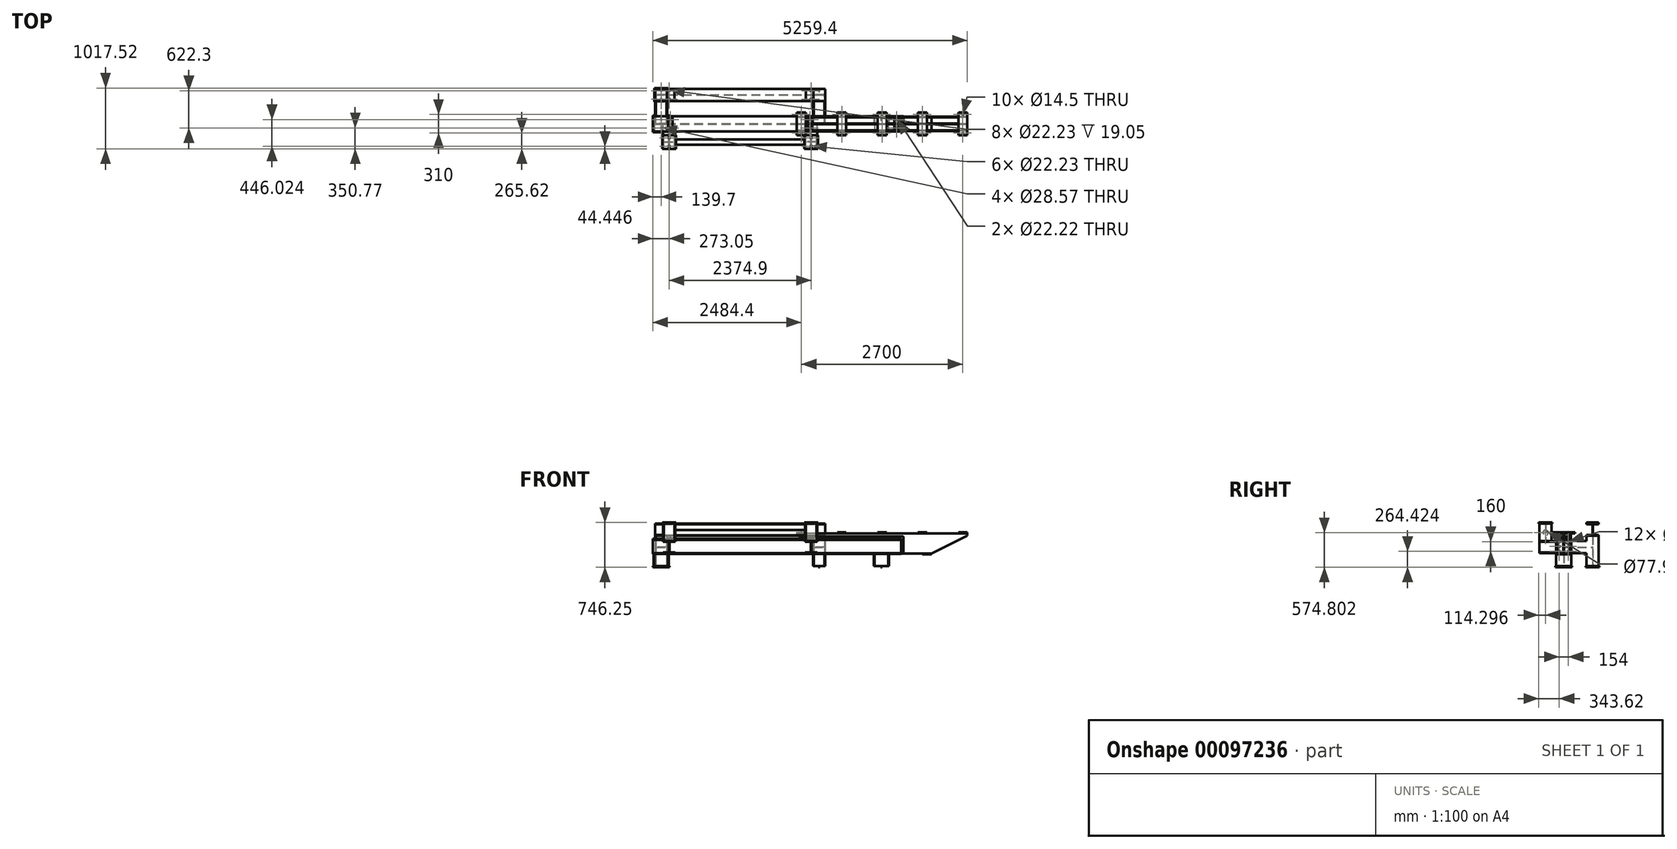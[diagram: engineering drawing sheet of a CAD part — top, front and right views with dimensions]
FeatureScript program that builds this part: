
annotation { "Feature Type Name" : "Feature", "Feature Type Description" : "" }
export const myFeature = defineFeature(function(context is Context, id is Id, definition is map)
    precondition{}
    {
        {
            var Q0;
            Q0=qCreatedBy(makeId("Top.planeOp"),FACE);
            var sketch = newSketch(context, id + "F0", { "sketchPlane" : qUnion([Q0])});
            skLineSegment(sketch, "E0.bottom", {"start": v(-1320.8, 241.3) * mm, "end": v(1320.8, 241.3) * mm, "construction": true});
            skLineSegment(sketch, "E0.top", {"start": v(-1320.8, -241.3) * mm, "end": v(1320.8, -241.3) * mm, "construction": true});
            skLineSegment(sketch, "E0.left", {"start": v(-1320.8, 241.3) * mm, "end": v(-1320.8, -241.3) * mm, "construction": true});
            skLineSegment(sketch, "E0.right", {"start": v(1320.8, 241.3) * mm, "end": v(1320.8, -241.3) * mm, "construction": true});
            skPoint(sketch, "E0.middle", {"position": v(0, 0) * mm});
            skLineSegment(sketch, "E1.bottom", {"start": v(-1435.1, 355.6) * mm, "end": v(-1206.5, 355.6) * mm});
            skLineSegment(sketch, "E1.top", {"start": v(-1435.1, 127) * mm, "end": v(-1206.5, 127) * mm});
            skLineSegment(sketch, "E1.left", {"start": v(-1435.1, 355.6) * mm, "end": v(-1435.1, 127) * mm});
            skLineSegment(sketch, "E1.right", {"start": v(-1206.5, 355.6) * mm, "end": v(-1206.5, 127) * mm});
            skPoint(sketch, "E1.middle", {"position": v(-1320.8, 241.3) * mm});
            skLineSegment(sketch, "E2", {"start": v(0, -413.23) * mm, "end": v(0, 639.03) * mm, "construction": true});
            skLineSegment(sketch, "E3", {"start": v(-1320.8, 355.6) * mm, "end": v(-1320.8, 127) * mm, "construction": true});
            skLineSegment(sketch, "E4", {"start": v(-1435.1, 241.3) * mm, "end": v(-1206.5, 241.3) * mm, "construction": true});
            skLineSegment(sketch, "E5.0", {"start": v(-1435.1, 311.15) * mm, "end": v(-1206.5, 311.15) * mm, "construction": true});
            skCircle(sketch, "E6", {"center": v(-1320.8, 311.15) * mm, "radius": 14.29 * mm});
            skCircle(sketch, "E7.MirrorC", {"center": v(-1320.8, 171.45) * mm, "radius": 14.29 * mm});
            skCircle(sketch, "E8.MirrorC", {"center": v(1320.8, 311.15) * mm, "radius": 14.29 * mm});
            skCircle(sketch, "E9.MirrorC", {"center": v(1320.8, 171.45) * mm, "radius": 14.29 * mm});
            skLineSegment(sketch, "E10.MirrorCS", {"start": v(1435.1, 311.15) * mm, "end": v(1206.5, 311.15) * mm, "construction": true});
            skLineSegment(sketch, "E11.MirrorCS", {"start": v(1435.1, 241.3) * mm, "end": v(1206.5, 241.3) * mm, "construction": true});
            skLineSegment(sketch, "E12.MirrorCS", {"start": v(1320.8, 355.6) * mm, "end": v(1320.8, 127) * mm, "construction": true});
            skLineSegment(sketch, "E13.MirrorCS", {"start": v(1435.1, 355.6) * mm, "end": v(1206.5, 355.6) * mm});
            skPoint(sketch, "E14.MirrorP", {"position": v(1320.8, 241.3) * mm});
            skLineSegment(sketch, "E15.MirrorCS", {"start": v(1206.5, 355.6) * mm, "end": v(1206.5, 127) * mm});
            skLineSegment(sketch, "E16.MirrorCS", {"start": v(1435.1, 127) * mm, "end": v(1206.5, 127) * mm});
            skLineSegment(sketch, "E17.MirrorCS", {"start": v(1435.1, 355.6) * mm, "end": v(1435.1, 127) * mm});
            skLineSegment(sketch, "E18.bottom", {"start": v(-1460.5, -381) * mm, "end": v(-1181.1, -381) * mm});
            skLineSegment(sketch, "E18.top", {"start": v(-1460.5, -101.6) * mm, "end": v(-1181.1, -101.6) * mm});
            skLineSegment(sketch, "E18.left", {"start": v(-1460.5, -381) * mm, "end": v(-1460.5, -101.6) * mm});
            skLineSegment(sketch, "E18.right", {"start": v(-1181.1, -381) * mm, "end": v(-1181.1, -101.6) * mm});
            skPoint(sketch, "E18.middle", {"position": v(-1320.8, -241.3) * mm});
            skLineSegment(sketch, "E19", {"start": v(-1320.8, -241.3) * mm, "end": v(-1460.5, -241.3) * mm, "construction": true});
            skLineSegment(sketch, "E20.0", {"start": v(-1320.8, -171.45) * mm, "end": v(-1460.5, -171.45) * mm, "construction": true});
            skCircle(sketch, "E21", {"center": v(-1320.8, -171.45) * mm, "radius": 14.29 * mm});
            skCircle(sketch, "E22.MirrorC", {"center": v(-1320.8, -311.15) * mm, "radius": 14.29 * mm});
            skLineSegment(sketch, "E23", {"start": v(-1320.8, -638.8) * mm, "end": v(-1320.8, -1011) * mm, "construction": true});
            skPoint(sketch, "E24.orphan", {"position": v(-1320.8, -381) * mm});
            skLineSegment(sketch, "E25.0", {"start": v(0, -638.8) * mm, "end": v(0, -1011) * mm, "construction": true});
            skLineSegment(sketch, "E26.0", {"start": v(1320.8, -638.8) * mm, "end": v(1320.8, -1011) * mm, "construction": true});
            skLineSegment(sketch, "E27.0", {"start": v(2362.2, -638.8) * mm, "end": v(2362.2, -1011) * mm, "construction": true});
            skLineSegment(sketch, "E28", {"start": v(-1320.8, -1011) * mm, "end": v(2362.2, -1011) * mm, "construction": true});
            skLineSegment(sketch, "E29", {"start": v(520.7, -1011) * mm, "end": v(520.7, -1354.57) * mm, "construction": true});
            skCircle(sketch, "E30.MirrorC", {"center": v(2362.2, -171.45) * mm, "radius": 14.29 * mm});
            skCircle(sketch, "E31.MirrorC", {"center": v(2362.2, -311.15) * mm, "radius": 14.29 * mm});
            skLineSegment(sketch, "E32.MirrorCS", {"start": v(2362.2, -171.45) * mm, "end": v(2501.9, -171.45) * mm, "construction": true});
            skLineSegment(sketch, "E33.MirrorCS", {"start": v(2501.9, -101.6) * mm, "end": v(2222.5, -101.6) * mm});
            skLineSegment(sketch, "E34.MirrorCS", {"start": v(2501.9, -381) * mm, "end": v(2222.5, -381) * mm});
            skLineSegment(sketch, "E35.MirrorCS", {"start": v(2362.2, -241.3) * mm, "end": v(2501.9, -241.3) * mm, "construction": true});
            skPoint(sketch, "E36.MirrorP", {"position": v(2362.2, -241.3) * mm});
            skLineSegment(sketch, "E37.MirrorCS", {"start": v(2222.5, -381) * mm, "end": v(2222.5, -101.6) * mm});
            skPoint(sketch, "E38.MirrorP", {"position": v(2362.2, -381) * mm});
            skLineSegment(sketch, "E39.MirrorCS", {"start": v(2501.9, -381) * mm, "end": v(2501.9, -101.6) * mm});
            skSolve(sketch);
        }
        {
            var Q0;
            Q0=makeQuery(id+"F0.imprint","IMPRINT",FACE,{"disambiguationData":[TD([[makeQuery(id+"F0.imprint","IMPRINT",EDGE,{"derivedFrom":sQuery(id+"F0.wireOp",EDGE,"E1.bottom")}),-1.0]])]});
            var Q1;
            Q1=makeQuery(id+"F0.imprint","IMPRINT",FACE,{"disambiguationData":[TD([[makeQuery(id+"F0.imprint","IMPRINT",EDGE,{"derivedFrom":sQuery(id+"F0.wireOp",EDGE,"E8.MirrorC")}),1.0]])]});
            var Q2;
            Q2=makeQuery(id+"F0.imprint","IMPRINT",FACE,{"disambiguationData":[TD([[makeQuery(id+"F0.imprint","IMPRINT",EDGE,{"derivedFrom":sQuery(id+"F0.wireOp",EDGE,"E30.MirrorC")}),1.0]])]});
            var Q3;
            Q3=makeQuery(id+"F0.imprint","IMPRINT",FACE,{"disambiguationData":[TD([[makeQuery(id+"F0.imprint","IMPRINT",EDGE,{"derivedFrom":sQuery(id+"F0.wireOp",EDGE,"E18.bottom")}),1.0]])]});
            extrude(context, id + "F1", {"entities" : qUnion([Q0, Q1, Q2, Q3]), "depth" : 19.05 * mm});
        }
        {
            var Q0;
            Q0=makeQuery(id+"F1.opExtrude","CAP_FACE",FACE,{"disambiguationData":[OSD([sQuery(id+"F0.wireOp",EDGE,"E1.bottom"),sQuery(id+"F0.wireOp",EDGE,"E1.top"),sQuery(id+"F0.wireOp",EDGE,"E1.left"),sQuery(id+"F0.wireOp",EDGE,"E1.right"),sQuery(id+"F0.wireOp",EDGE,"E6"),sQuery(id+"F0.wireOp",EDGE,"E7.MirrorC")])],"isStart":false});
            var sketch = newSketch(context, id + "F2", { "sketchPlane" : qUnion([Q0])});
            skLineSegment(sketch, "E40.0", {"start": v(-1435.1, 241.3) * mm, "end": v(-1206.5, 241.3) * mm, "construction": true});
            skLineSegment(sketch, "E41.0", {"start": v(-1320.8, 355.6) * mm, "end": v(-1320.8, 127) * mm, "construction": true});
            skLineSegment(sketch, "E42.bottom", {"start": v(-1422.4, 342.9) * mm, "end": v(-1411.35, 342.9) * mm});
            skLineSegment(sketch, "E42.top", {"start": v(-1422.4, 139.7) * mm, "end": v(-1411.35, 139.7) * mm});
            skLineSegment(sketch, "E42.left", {"start": v(-1422.4, 342.9) * mm, "end": v(-1422.4, 139.7) * mm});
            skLineSegment(sketch, "E42.right", {"start": v(-1219.2, 342.9) * mm, "end": v(-1219.2, 139.7) * mm, "construction": true});
            skPoint(sketch, "E42.middle", {"position": v(-1320.8, 241.3) * mm});
            skLineSegment(sketch, "E43.0", {"start": v(-1411.35, 342.9) * mm, "end": v(-1411.35, 251.27) * mm});
            skLineSegment(sketch, "E44.trimOffspring", {"start": v(-1405, 237.68) * mm, "end": v(-1320.8, 237.68) * mm});
            skLineSegment(sketch, "E45.MirrorCS", {"start": v(-1405, 244.92) * mm, "end": v(-1320.8, 244.92) * mm});
            skLineSegment(sketch, "E46.trimOffspring", {"start": v(-1411.35, 231.33) * mm, "end": v(-1411.35, 139.7) * mm});
            skPoint(sketch, "E47.visualSharp", {"position": v(-1411.35, 244.92) * mm});
            skArc(sketch, "E47.filletArc", {"start": v(-1411.35, 251.27) * mm, "mid": v(-1409.5, 246.78) * mm, "end": v(-1405, 244.92) * mm});
            skPoint(sketch, "E48.visualSharp", {"position": v(-1411.35, 237.68) * mm});
            skArc(sketch, "E48.filletArc", {"start": v(-1405, 237.68) * mm, "mid": v(-1409.5, 235.82) * mm, "end": v(-1411.35, 231.33) * mm});
            skArc(sketch, "E49.MirrorCS", {"start": v(-1236.6, 237.68) * mm, "mid": v(-1232.1, 235.82) * mm, "end": v(-1230.25, 231.33) * mm});
            skArc(sketch, "E50.MirrorCS", {"start": v(-1230.25, 251.27) * mm, "mid": v(-1232.1, 246.78) * mm, "end": v(-1236.6, 244.92) * mm});
            skPoint(sketch, "E51.MirrorP", {"position": v(-1230.25, 237.68) * mm});
            skPoint(sketch, "E52.MirrorP", {"position": v(-1230.25, 244.92) * mm});
            skLineSegment(sketch, "E53.MirrorCS", {"start": v(-1230.25, 342.9) * mm, "end": v(-1230.25, 251.27) * mm});
            skLineSegment(sketch, "E54.MirrorCS", {"start": v(-1236.6, 237.68) * mm, "end": v(-1320.8, 237.68) * mm});
            skLineSegment(sketch, "E55.MirrorCS", {"start": v(-1236.6, 244.92) * mm, "end": v(-1320.8, 244.92) * mm});
            skLineSegment(sketch, "E56.MirrorCS", {"start": v(-1219.2, 139.7) * mm, "end": v(-1230.25, 139.7) * mm});
            skLineSegment(sketch, "E57.MirrorCS", {"start": v(-1230.25, 231.33) * mm, "end": v(-1230.25, 139.7) * mm});
            skLineSegment(sketch, "E58.MirrorCS", {"start": v(-1219.2, 342.9) * mm, "end": v(-1230.25, 342.9) * mm});
            skLineSegment(sketch, "E59.MirrorCS", {"start": v(-1219.2, 342.9) * mm, "end": v(-1219.2, 139.7) * mm});
            skLineSegment(sketch, "E60.0", {"start": v(0, -413.23) * mm, "end": v(0, 639.03) * mm, "construction": true});
            skArc(sketch, "E61.MirrorCS", {"start": v(1411.35, 251.27) * mm, "mid": v(1409.5, 246.78) * mm, "end": v(1405, 244.92) * mm});
            skArc(sketch, "E62.MirrorCS", {"start": v(1405, 237.68) * mm, "mid": v(1409.5, 235.82) * mm, "end": v(1411.35, 231.33) * mm});
            skLineSegment(sketch, "E63.MirrorCS", {"start": v(1236.6, 244.92) * mm, "end": v(1320.8, 244.92) * mm});
            skArc(sketch, "E64.MirrorCS", {"start": v(1236.6, 237.68) * mm, "mid": v(1232.1, 235.82) * mm, "end": v(1230.25, 231.33) * mm});
            skLineSegment(sketch, "E65.MirrorCS", {"start": v(1422.4, 139.7) * mm, "end": v(1411.35, 139.7) * mm});
            skLineSegment(sketch, "E66.MirrorCS", {"start": v(1422.4, 342.9) * mm, "end": v(1411.35, 342.9) * mm});
            skArc(sketch, "E67.MirrorCS", {"start": v(1230.25, 251.27) * mm, "mid": v(1232.1, 246.78) * mm, "end": v(1236.6, 244.92) * mm});
            skLineSegment(sketch, "E68.MirrorCS", {"start": v(1236.6, 237.68) * mm, "end": v(1320.8, 237.68) * mm});
            skLineSegment(sketch, "E69.MirrorCS", {"start": v(1435.1, 241.3) * mm, "end": v(1206.5, 241.3) * mm, "construction": true});
            skLineSegment(sketch, "E70.MirrorCS", {"start": v(1405, 237.68) * mm, "end": v(1320.8, 237.68) * mm});
            skLineSegment(sketch, "E71.MirrorCS", {"start": v(1219.2, 342.9) * mm, "end": v(1230.25, 342.9) * mm});
            skLineSegment(sketch, "E72.MirrorCS", {"start": v(1219.2, 139.7) * mm, "end": v(1230.25, 139.7) * mm});
            skLineSegment(sketch, "E73.MirrorCS", {"start": v(1411.35, 342.9) * mm, "end": v(1411.35, 251.27) * mm});
            skLineSegment(sketch, "E74.MirrorCS", {"start": v(1405, 244.92) * mm, "end": v(1320.8, 244.92) * mm});
            skLineSegment(sketch, "E75.MirrorCS", {"start": v(1411.35, 231.33) * mm, "end": v(1411.35, 139.7) * mm});
            skPoint(sketch, "E76.MirrorP", {"position": v(1411.35, 237.68) * mm});
            skPoint(sketch, "E77.MirrorP", {"position": v(1320.8, 241.3) * mm});
            skLineSegment(sketch, "E78.MirrorCS", {"start": v(1219.2, 342.9) * mm, "end": v(1219.2, 139.7) * mm, "construction": true});
            skLineSegment(sketch, "E79.MirrorCS", {"start": v(1422.4, 342.9) * mm, "end": v(1422.4, 139.7) * mm});
            skPoint(sketch, "E80.MirrorP", {"position": v(1230.25, 237.68) * mm});
            skLineSegment(sketch, "E81.MirrorCS", {"start": v(1320.8, 355.6) * mm, "end": v(1320.8, 127) * mm, "construction": true});
            skPoint(sketch, "E82.MirrorP", {"position": v(1411.35, 244.92) * mm});
            skLineSegment(sketch, "E83.MirrorCS", {"start": v(1219.2, 342.9) * mm, "end": v(1219.2, 139.7) * mm});
            skLineSegment(sketch, "E84.MirrorCS", {"start": v(1230.25, 231.33) * mm, "end": v(1230.25, 139.7) * mm});
            skLineSegment(sketch, "E85.MirrorCS", {"start": v(1230.25, 342.9) * mm, "end": v(1230.25, 251.27) * mm});
            skPoint(sketch, "E86.MirrorP", {"position": v(1230.25, 244.92) * mm});
            skSolve(sketch);
        }
        {
            var Q0;
            Q0=qSketchRegion(id+"F2",true);
            extrude(context, id + "F3", {"entities" : qUnion([Q0]), "depth" : 504.95 * mm});
        }
        {
            var Q0;
            Q0=makeQuery(id+"F3.opExtrude","SWEPT_FACE",FACE,{"disambiguationData":[OSD([sQuery(id+"F2.wireOp",EDGE,"E79.MirrorCS")])]});
            var sketch = newSketch(context, id + "F4", { "sketchPlane" : qUnion([Q0])});
            skLineSegment(sketch, "E87.bottom", {"start": v(139.7, 524) * mm, "end": v(342.9, 524) * mm});
            skLineSegment(sketch, "E87.top", {"start": v(139.7, 727.2) * mm, "end": v(342.9, 727.2) * mm});
            skLineSegment(sketch, "E87.left", {"start": v(139.7, 524) * mm, "end": v(139.7, 535.05) * mm});
            skLineSegment(sketch, "E87.right", {"start": v(342.9, 524) * mm, "end": v(342.9, 535.05) * mm});
            skLineSegment(sketch, "E88", {"start": v(241.3, 727.2) * mm, "end": v(241.3, 524) * mm, "construction": true});
            skLineSegment(sketch, "E89.0", {"start": v(237.68, 709.8) * mm, "end": v(237.68, 541.4) * mm});
            skLineSegment(sketch, "E90.MirrorCS", {"start": v(244.92, 709.8) * mm, "end": v(244.92, 541.4) * mm});
            skLineSegment(sketch, "E91.0", {"start": v(139.7, 716.15) * mm, "end": v(231.33, 716.15) * mm});
            skLineSegment(sketch, "E92.0", {"start": v(139.7, 535.05) * mm, "end": v(231.33, 535.05) * mm});
            skLineSegment(sketch, "E93.trimOffspring", {"start": v(251.27, 716.15) * mm, "end": v(342.9, 716.15) * mm});
            skLineSegment(sketch, "E94.trimOffspring", {"start": v(251.27, 535.05) * mm, "end": v(342.9, 535.05) * mm});
            skLineSegment(sketch, "E95.trimOffspring", {"start": v(139.7, 716.15) * mm, "end": v(139.7, 727.2) * mm});
            skLineSegment(sketch, "E96.trimOffspring", {"start": v(342.9, 716.15) * mm, "end": v(342.9, 727.2) * mm});
            skPoint(sketch, "E97.newPointB", {"position": v(237.68, 524) * mm});
            skArc(sketch, "E97.filletArc", {"start": v(231.33, 535.05) * mm, "mid": v(235.82, 536.91) * mm, "end": v(237.68, 541.4) * mm});
            skPoint(sketch, "E98.newPointA", {"position": v(244.92, 524) * mm});
            skArc(sketch, "E98.filletArc", {"start": v(244.92, 541.4) * mm, "mid": v(246.78, 536.91) * mm, "end": v(251.27, 535.05) * mm});
            skPoint(sketch, "E99.newPointA", {"position": v(237.68, 727.2) * mm});
            skArc(sketch, "E99.filletArc", {"start": v(237.68, 709.8) * mm, "mid": v(235.82, 714.3) * mm, "end": v(231.33, 716.15) * mm});
            skPoint(sketch, "E100.newPointA", {"position": v(244.92, 727.2) * mm});
            skArc(sketch, "E100.filletArc", {"start": v(251.27, 716.15) * mm, "mid": v(246.78, 714.3) * mm, "end": v(244.92, 709.8) * mm});
            skSolve(sketch);
        }
        {
            var Q0;
            Q0=qSketchRegion(id+"F4",true);
            var Q1;
            Q1=makeQuery(id+"F3.opExtrude","SWEPT_FACE",FACE,{"disambiguationData":[OSD([sQuery(id+"F2.wireOp",EDGE,"E42.left")])]});
            extrude(context, id + "F5", {"entities" : qUnion([Q0]), "endBound" : BoundingType.UP_TO_SURFACE, "oppositeDirection" : true, "endBoundEntityFace" : qUnion([Q1]), "depth" : 25.4 * mm});
        }
        {
            var Q0;
            Q0=makeQuery(id+"F5.opExtrude","SWEPT_FACE",FACE,{"disambiguationData":[OSD([sQuery(id+"F4.wireOp",EDGE,"E87.top")])]});
            var sketch = newSketch(context, id + "F6", { "sketchPlane" : qUnion([Q0])});
            skLineSegment(sketch, "E101.0", {"start": v(0, -413.23) * mm, "end": v(0, 639.03) * mm, "construction": true});
            skLineSegment(sketch, "E102.0", {"start": v(-1187.45, -413.23) * mm, "end": v(-1187.45, 639.03) * mm, "construction": true});
            skLineSegment(sketch, "E103.0", {"start": v(-1225.55, 139.7) * mm, "end": v(-1225.55, 342.9) * mm});
            skLineSegment(sketch, "E104.0", {"start": v(-1098.55, 139.7) * mm, "end": v(-1098.55, 342.9) * mm});
            skLineSegment(sketch, "E105.0", {"start": v(-1422.4, 342.9) * mm, "end": v(1422.4, 342.9) * mm, "construction": true});
            skLineSegment(sketch, "E106.0.0", {"start": v(1225.55, 342.9) * mm, "end": v(-1225.55, 342.9) * mm});
            skLineSegment(sketch, "E106.0.1", {"start": v(-1422.4, 342.9) * mm, "end": v(-1422.4, 139.7) * mm});
            skLineSegment(sketch, "E106.0.2", {"start": v(-1225.55, 139.7) * mm, "end": v(-1098.55, 139.7) * mm});
            skLineSegment(sketch, "E106.0.3", {"start": v(1422.4, 139.7) * mm, "end": v(1422.4, 342.9) * mm});
            skLineSegment(sketch, "E107.trimOffspring", {"start": v(0, 139.7) * mm, "end": v(1225.55, 139.7) * mm});
            skLineSegment(sketch, "E108.0", {"start": v(-1320.8, 241.3) * mm, "end": v(1320.8, 241.3) * mm, "construction": true});
            skLineSegment(sketch, "E109.0", {"start": v(-1320.8, 311.15) * mm, "end": v(1320.8, 311.15) * mm, "construction": true});
            skCircle(sketch, "E110", {"center": v(-1187.45, 311.15) * mm, "radius": 11.11 * mm});
            skCircle(sketch, "E111.MirrorC", {"center": v(-1187.45, 171.45) * mm, "radius": 11.11 * mm});
            skCircle(sketch, "E112.MirrorC", {"center": v(1187.45, 311.15) * mm, "radius": 11.11 * mm});
            skCircle(sketch, "E113.MirrorC", {"center": v(1187.45, 171.45) * mm, "radius": 11.11 * mm});
            skLineSegment(sketch, "E114.MirrorCS", {"start": v(1225.55, 139.7) * mm, "end": v(1098.55, 139.7) * mm});
            skLineSegment(sketch, "E115.MirrorCS", {"start": v(1225.55, 139.7) * mm, "end": v(1225.55, 342.9) * mm});
            skLineSegment(sketch, "E116.MirrorCS", {"start": v(1098.55, 139.7) * mm, "end": v(1098.55, 342.9) * mm});
            skSolve(sketch);
        }
        {
            var Q0;
            Q0=qSketchRegion(id+"F6",true);
            extrude(context, id + "F7", {"entities" : qUnion([Q0]), "operationType" : NewBodyOperationType.ADD, "depth" : 19.05 * mm});
        }
        {
            var Q0;
            Q0=makeQuery(id+"F3.opExtrude","SWEPT_FACE",FACE,{"disambiguationData":[OSD([sQuery(id+"F2.wireOp",EDGE,"E44.trimOffspring"),sQuery(id+"F2.wireOp",EDGE,"E54.MirrorCS")])]});
            var sketch = newSketch(context, id + "F8", { "sketchPlane" : qUnion([Q0])});
            skLineSegment(sketch, "E117.0", {"start": v(-1460.5, 0) * mm, "end": v(-1181.1, 0) * mm, "construction": true});
            skLineSegment(sketch, "E118", {"start": v(-1320.8, 0) * mm, "end": v(-1320.8, 868.41) * mm, "construction": true});
            skLineSegment(sketch, "E119.0", {"start": v(-1422.4, 231.65) * mm, "end": v(-1411.35, 231.65) * mm});
            skLineSegment(sketch, "E120.0", {"start": v(-1422.4, 434.85) * mm, "end": v(-1411.35, 434.85) * mm});
            skLineSegment(sketch, "E121", {"start": v(-1422.4, 434.85) * mm, "end": v(-1422.4, 231.65) * mm});
            skLineSegment(sketch, "E122.0", {"start": v(-1411.35, 434.85) * mm, "end": v(-1411.35, 342.77) * mm});
            skLineSegment(sketch, "E123", {"start": v(-1411.35, 333.25) * mm, "end": v(-1320.8, 333.25) * mm, "construction": true});
            skLineSegment(sketch, "E124.0", {"start": v(-1405, 336.42) * mm, "end": v(-1320.8, 336.42) * mm});
            skLineSegment(sketch, "E125.MirrorCS", {"start": v(-1410.08, 330.07) * mm, "end": v(-1320.8, 330.07) * mm});
            skLineSegment(sketch, "E126.trimOffspring", {"start": v(-1411.35, 328.8) * mm, "end": v(-1411.35, 231.65) * mm});
            skPoint(sketch, "E127.newPointA", {"position": v(-1411.35, 336.42) * mm});
            skArc(sketch, "E127.filletArc", {"start": v(-1411.35, 342.77) * mm, "mid": v(-1409.5, 338.28) * mm, "end": v(-1405, 336.42) * mm});
            skPoint(sketch, "E128.visualSharp", {"position": v(-1411.35, 330.07) * mm});
            skArc(sketch, "E128.filletArc", {"start": v(-1410.08, 330.07) * mm, "mid": v(-1410.98, 329.7) * mm, "end": v(-1411.35, 328.8) * mm});
            skArc(sketch, "E129.MirrorCS", {"start": v(-1231.52, 330.07) * mm, "mid": v(-1230.62, 329.7) * mm, "end": v(-1230.25, 328.8) * mm});
            skArc(sketch, "E130.MirrorCS", {"start": v(-1230.25, 342.77) * mm, "mid": v(-1232.1, 338.28) * mm, "end": v(-1236.6, 336.42) * mm});
            skLineSegment(sketch, "E131.MirrorCS", {"start": v(-1219.2, 231.65) * mm, "end": v(-1230.25, 231.65) * mm});
            skLineSegment(sketch, "E132.MirrorCS", {"start": v(-1219.2, 434.85) * mm, "end": v(-1230.25, 434.85) * mm});
            skPoint(sketch, "E133.MirrorP", {"position": v(-1230.25, 336.42) * mm});
            skPoint(sketch, "E134.MirrorP", {"position": v(-1230.25, 330.07) * mm});
            skLineSegment(sketch, "E135.MirrorCS", {"start": v(-1230.25, 328.8) * mm, "end": v(-1230.25, 231.65) * mm});
            skLineSegment(sketch, "E136.MirrorCS", {"start": v(-1231.52, 330.07) * mm, "end": v(-1320.8, 330.07) * mm});
            skLineSegment(sketch, "E137.MirrorCS", {"start": v(-1219.2, 434.85) * mm, "end": v(-1219.2, 231.65) * mm});
            skLineSegment(sketch, "E138.MirrorCS", {"start": v(-1230.25, 434.85) * mm, "end": v(-1230.25, 342.77) * mm});
            skLineSegment(sketch, "E139.MirrorCS", {"start": v(-1230.25, 333.25) * mm, "end": v(-1320.8, 333.25) * mm, "construction": true});
            skLineSegment(sketch, "E140.MirrorCS", {"start": v(-1236.6, 336.42) * mm, "end": v(-1320.8, 336.42) * mm});
            skLineSegment(sketch, "E141", {"start": v(0, -179.83) * mm, "end": v(0, 965.66) * mm, "construction": true});
            skArc(sketch, "E142.MirrorCS", {"start": v(1411.35, 342.77) * mm, "mid": v(1409.5, 338.28) * mm, "end": v(1405, 336.42) * mm});
            skArc(sketch, "E143.MirrorCS", {"start": v(1410.08, 330.07) * mm, "mid": v(1410.98, 329.7) * mm, "end": v(1411.35, 328.8) * mm});
            skArc(sketch, "E144.MirrorCS", {"start": v(1230.25, 342.77) * mm, "mid": v(1232.1, 338.28) * mm, "end": v(1236.6, 336.42) * mm});
            skArc(sketch, "E145.MirrorCS", {"start": v(1231.52, 330.07) * mm, "mid": v(1230.62, 329.7) * mm, "end": v(1230.25, 328.8) * mm});
            skLineSegment(sketch, "E146.MirrorCS", {"start": v(1411.35, 333.25) * mm, "end": v(1320.8, 333.25) * mm, "construction": true});
            skLineSegment(sketch, "E147.MirrorCS", {"start": v(1219.2, 231.65) * mm, "end": v(1230.25, 231.65) * mm});
            skLineSegment(sketch, "E148.MirrorCS", {"start": v(1219.2, 434.85) * mm, "end": v(1230.25, 434.85) * mm});
            skLineSegment(sketch, "E149.MirrorCS", {"start": v(1422.4, 231.65) * mm, "end": v(1411.35, 231.65) * mm});
            skLineSegment(sketch, "E150.MirrorCS", {"start": v(1422.4, 434.85) * mm, "end": v(1411.35, 434.85) * mm});
            skLineSegment(sketch, "E151.MirrorCS", {"start": v(1405, 336.42) * mm, "end": v(1320.8, 336.42) * mm});
            skLineSegment(sketch, "E152.MirrorCS", {"start": v(1410.08, 330.07) * mm, "end": v(1320.8, 330.07) * mm});
            skLineSegment(sketch, "E153.MirrorCS", {"start": v(1230.25, 333.25) * mm, "end": v(1320.8, 333.25) * mm, "construction": true});
            skLineSegment(sketch, "E154.MirrorCS", {"start": v(1231.52, 330.07) * mm, "end": v(1320.8, 330.07) * mm});
            skLineSegment(sketch, "E155.MirrorCS", {"start": v(1236.6, 336.42) * mm, "end": v(1320.8, 336.42) * mm});
            skLineSegment(sketch, "E156.MirrorCS", {"start": v(1411.35, 328.8) * mm, "end": v(1411.35, 231.65) * mm});
            skPoint(sketch, "E157.MirrorP", {"position": v(1411.35, 330.07) * mm});
            skPoint(sketch, "E158.MirrorP", {"position": v(1411.35, 336.42) * mm});
            skLineSegment(sketch, "E159.MirrorCS", {"start": v(1422.4, 434.85) * mm, "end": v(1422.4, 231.65) * mm});
            skLineSegment(sketch, "E160.MirrorCS", {"start": v(1411.35, 434.85) * mm, "end": v(1411.35, 342.77) * mm});
            skLineSegment(sketch, "E161.MirrorCS", {"start": v(1230.25, 434.85) * mm, "end": v(1230.25, 342.77) * mm});
            skLineSegment(sketch, "E162.MirrorCS", {"start": v(1230.25, 328.8) * mm, "end": v(1230.25, 231.65) * mm});
            skPoint(sketch, "E163.MirrorP", {"position": v(1230.25, 330.07) * mm});
            skPoint(sketch, "E164.MirrorP", {"position": v(1230.25, 336.42) * mm});
            skLineSegment(sketch, "E165.MirrorCS", {"start": v(1219.2, 434.85) * mm, "end": v(1219.2, 231.65) * mm});
            skSolve(sketch);
        }
        {
            var Q0;
            Q0=qSketchRegion(id+"F8",true);
            extrude(context, id + "F9", {"entities" : qUnion([Q0]), "operationType" : NewBodyOperationType.ADD, "depth" : 482.6 * mm});
        }
        {
            var Q0;
            Q0=qCreatedBy(makeId("Right.planeOp"),FACE);
            cPlane(context, id + "F10", {"entities" : qUnion([Q0]), "cplaneType" : CPlaneType.OFFSET, "offset" : 2692.4 * mm, "width" : 152.4 * mm, "height" : 152.4 * mm});
        }
        {
            var Q0;
            Q0=qCreatedBy(id+"F10.planeOp",FACE);
            var sketch = newSketch(context, id + "F11", { "sketchPlane" : qUnion([Q0])});
            skLineSegment(sketch, "E166.0", {"start": v(-381, 19.05) * mm, "end": v(-101.6, 19.05) * mm, "construction": true});
            skLineSegment(sketch, "E167", {"start": v(-241.3, 19.05) * mm, "end": v(-241.3, 468.37) * mm, "construction": true});
            skLineSegment(sketch, "E168.0", {"start": v(-381, 217.42) * mm, "end": v(-101.6, 217.42) * mm, "construction": true});
            skLineSegment(sketch, "E169.bottom", {"start": v(-368.3, 217.42) * mm, "end": v(-114.3, 217.42) * mm});
            skLineSegment(sketch, "E169.top", {"start": v(-368.3, 471.42) * mm, "end": v(-114.3, 471.42) * mm});
            skLineSegment(sketch, "E169.left", {"start": v(-368.3, 217.42) * mm, "end": v(-368.3, 231.65) * mm});
            skLineSegment(sketch, "E169.right", {"start": v(-114.3, 217.42) * mm, "end": v(-114.3, 231.65) * mm});
            skLineSegment(sketch, "E170.0", {"start": v(-368.3, 457.2) * mm, "end": v(-254, 457.2) * mm});
            skLineSegment(sketch, "E171.0", {"start": v(-368.3, 231.65) * mm, "end": v(-254, 231.65) * mm});
            skLineSegment(sketch, "E172.0", {"start": v(-234.95, 238) * mm, "end": v(-234.95, 450.85) * mm});
            skLineSegment(sketch, "E173.MirrorCS", {"start": v(-247.65, 238) * mm, "end": v(-247.65, 450.85) * mm});
            skLineSegment(sketch, "E174.trimOffspring", {"start": v(-368.3, 457.2) * mm, "end": v(-368.3, 471.42) * mm});
            skLineSegment(sketch, "E175.trimOffspring", {"start": v(-114.3, 457.2) * mm, "end": v(-114.3, 471.42) * mm});
            skLineSegment(sketch, "E176.trimOffspring", {"start": v(-228.6, 457.2) * mm, "end": v(-114.3, 457.2) * mm});
            skLineSegment(sketch, "E177.trimOffspring", {"start": v(-228.6, 231.65) * mm, "end": v(-114.3, 231.65) * mm});
            skPoint(sketch, "E178.newPointB", {"position": v(-247.65, 468.37) * mm});
            skArc(sketch, "E178.filletArc", {"start": v(-247.65, 450.85) * mm, "mid": v(-249.5, 455.34) * mm, "end": v(-254, 457.2) * mm});
            skPoint(sketch, "E179.newPointB", {"position": v(-234.95, 468.37) * mm});
            skArc(sketch, "E179.filletArc", {"start": v(-228.6, 457.2) * mm, "mid": v(-233.1, 455.34) * mm, "end": v(-234.95, 450.85) * mm});
            skPoint(sketch, "E180.newPointB", {"position": v(-234.95, 19.05) * mm});
            skArc(sketch, "E180.filletArc", {"start": v(-234.95, 238) * mm, "mid": v(-233.1, 233.5) * mm, "end": v(-228.6, 231.65) * mm});
            skPoint(sketch, "E181.newPointA", {"position": v(-247.65, 19.05) * mm});
            skArc(sketch, "E181.filletArc", {"start": v(-254, 231.65) * mm, "mid": v(-249.5, 233.5) * mm, "end": v(-247.65, 238) * mm});
            skSolve(sketch);
        }
        {
            var Q0;
            Q0=qSketchRegion(id+"F11",true);
            extrude(context, id + "F12", {"entities" : qUnion([Q0]), "oppositeDirection" : true, "depth" : 4152.9 * mm});
        }
        {
            var Q0;
            Q0=makeQuery(id+"F1.opExtrude","CAP_FACE",FACE,{"disambiguationData":[OSD([sQuery(id+"F0.wireOp",EDGE,"E18.bottom"),sQuery(id+"F0.wireOp",EDGE,"E18.top"),sQuery(id+"F0.wireOp",EDGE,"E18.left"),sQuery(id+"F0.wireOp",EDGE,"E18.right"),sQuery(id+"F0.wireOp",EDGE,"E21"),sQuery(id+"F0.wireOp",EDGE,"E22.MirrorC")])],"isStart":false});
            var sketch = newSketch(context, id + "F13", { "sketchPlane" : qUnion([Q0])});
            skLineSegment(sketch, "E182.bottom", {"start": v(-1447.8, -114.3) * mm, "end": v(-1433.58, -114.3) * mm});
            skLineSegment(sketch, "E182.top", {"start": v(-1447.8, -368.3) * mm, "end": v(-1433.58, -368.3) * mm});
            skLineSegment(sketch, "E182.left", {"start": v(-1447.8, -114.3) * mm, "end": v(-1447.8, -368.3) * mm});
            skLineSegment(sketch, "E182.right", {"start": v(-1193.8, -114.3) * mm, "end": v(-1193.8, -368.3) * mm});
            skPoint(sketch, "E182.middle", {"position": v(-1320.8, -241.3) * mm});
            skLineSegment(sketch, "E183.0", {"start": v(-1433.58, -114.3) * mm, "end": v(-1433.58, -236.98) * mm});
            skLineSegment(sketch, "E184.0", {"start": v(-1208.02, -114.3) * mm, "end": v(-1208.02, -236.98) * mm});
            skLineSegment(sketch, "E185.trimOffspring", {"start": v(-1208.02, -114.3) * mm, "end": v(-1193.8, -114.3) * mm});
            skLineSegment(sketch, "E186.trimOffspring", {"start": v(-1208.02, -368.3) * mm, "end": v(-1193.8, -368.3) * mm});
            skLineSegment(sketch, "E187.0", {"start": v(-1208.02, -236.98) * mm, "end": v(-1433.58, -236.98) * mm});
            skLineSegment(sketch, "E188.MirrorCS", {"start": v(-1208.02, -245.62) * mm, "end": v(-1433.58, -245.62) * mm});
            skPoint(sketch, "E189.orphan", {"position": v(-1460.5, -236.98) * mm});
            skPoint(sketch, "E190.orphan", {"position": v(-1460.5, -245.62) * mm});
            skLineSegment(sketch, "E191.trimOffspring", {"start": v(-1433.58, -245.62) * mm, "end": v(-1433.58, -368.3) * mm});
            skPoint(sketch, "E192.orphan", {"position": v(-1320.8, -236.98) * mm});
            skPoint(sketch, "E193.orphan", {"position": v(-1320.8, -245.62) * mm});
            skLineSegment(sketch, "E194.trimOffspring", {"start": v(-1208.02, -245.62) * mm, "end": v(-1208.02, -368.3) * mm});
            skLineSegment(sketch, "E195.MirrorCS", {"start": v(2489.2, -368.3) * mm, "end": v(2474.98, -368.3) * mm});
            skLineSegment(sketch, "E196.MirrorCS", {"start": v(2489.2, -114.3) * mm, "end": v(2474.98, -114.3) * mm});
            skLineSegment(sketch, "E197.MirrorCS", {"start": v(2249.42, -368.3) * mm, "end": v(2235.2, -368.3) * mm});
            skLineSegment(sketch, "E198.MirrorCS", {"start": v(2249.42, -114.3) * mm, "end": v(2235.2, -114.3) * mm});
            skPoint(sketch, "E199.MirrorP", {"position": v(2362.2, -245.62) * mm});
            skPoint(sketch, "E200.MirrorP", {"position": v(2362.2, -236.98) * mm});
            skLineSegment(sketch, "E201.MirrorCS", {"start": v(2249.42, -245.62) * mm, "end": v(2474.98, -245.62) * mm});
            skPoint(sketch, "E202.MirrorP", {"position": v(2501.9, -236.98) * mm});
            skLineSegment(sketch, "E203.MirrorCS", {"start": v(2249.42, -236.98) * mm, "end": v(2474.98, -236.98) * mm});
            skPoint(sketch, "E204.MirrorP", {"position": v(2362.2, -241.3) * mm});
            skPoint(sketch, "E205.MirrorP", {"position": v(2501.9, -245.62) * mm});
            skLineSegment(sketch, "E206.MirrorCS", {"start": v(2249.42, -245.62) * mm, "end": v(2249.42, -368.3) * mm});
            skLineSegment(sketch, "E207.MirrorCS", {"start": v(2474.98, -245.62) * mm, "end": v(2474.98, -368.3) * mm});
            skLineSegment(sketch, "E208.MirrorCS", {"start": v(2249.42, -114.3) * mm, "end": v(2249.42, -236.98) * mm});
            skLineSegment(sketch, "E209.MirrorCS", {"start": v(2474.98, -114.3) * mm, "end": v(2474.98, -236.98) * mm});
            skLineSegment(sketch, "E210.MirrorCS", {"start": v(2235.2, -114.3) * mm, "end": v(2235.2, -368.3) * mm});
            skLineSegment(sketch, "E211.MirrorCS", {"start": v(2489.2, -114.3) * mm, "end": v(2489.2, -368.3) * mm});
            skSolve(sketch);
        }
        {
            var Q0;
            Q0=qSketchRegion(id+"F13",true);
            extrude(context, id + "F14", {"entities" : qUnion([Q0]), "depth" : 198.37 * mm});
        }
        {
            var Q0;
            Q0=makeQuery(id+"F12.opExtrude","SWEPT_FACE",FACE,{"disambiguationData":[OSD([sQuery(id+"F11.wireOp",EDGE,"E169.top")])]});
            var sketch = newSketch(context, id + "F15", { "sketchPlane" : qUnion([Q0])});
            skLineSegment(sketch, "E212.0", {"start": v(-1615.4, -241.3) * mm, "end": v(2831.5, -241.3) * mm, "construction": true});
            skLineSegment(sketch, "E213.0", {"start": v(0, -413.23) * mm, "end": v(0, 639.03) * mm, "construction": true});
            skPoint(sketch, "E214.orphan", {"position": v(-1320.8, -241.3) * mm});
            skLineSegment(sketch, "E215.0", {"start": v(-1168.4, -689.85) * mm, "end": v(-1168.4, 639.03) * mm, "construction": true});
            skLineSegment(sketch, "E216.0", {"start": v(-1130.3, -355.6) * mm, "end": v(-1130.3, -127) * mm});
            skLineSegment(sketch, "E217.0", {"start": v(-1206.5, -127) * mm, "end": v(-1130.3, -127) * mm});
            skLineSegment(sketch, "E218.0", {"start": v(-1615.4, -171.45) * mm, "end": v(2831.5, -171.45) * mm, "construction": true});
            skLineSegment(sketch, "E219.MirrorCS", {"start": v(-1206.5, -355.6) * mm, "end": v(-1130.3, -355.6) * mm});
            skLineSegment(sketch, "E220.MirrorCS", {"start": v(-1206.5, -355.6) * mm, "end": v(-1206.5, -127) * mm});
            skPoint(sketch, "E221.orphan", {"position": v(-1130.3, 639.03) * mm});
            skPoint(sketch, "E222.orphan", {"position": v(-1206.5, 639.03) * mm});
            skPoint(sketch, "E223.orphan", {"position": v(-1615.4, -127) * mm});
            skPoint(sketch, "E224.orphan", {"position": v(-1615.4, -355.6) * mm});
            skPoint(sketch, "E225.orphan", {"position": v(-1206.5, -689.85) * mm});
            skPoint(sketch, "E226.orphan", {"position": v(-1130.3, -689.85) * mm});
            skCircle(sketch, "E227", {"center": v(-1168.4, -171.45) * mm, "radius": 11.11 * mm});
            skCircle(sketch, "E228.MirrorC", {"center": v(-1168.4, -311.15) * mm, "radius": 11.11 * mm});
            skLineSegment(sketch, "E229.1.0.0", {"start": v(1130.3, -355.6) * mm, "end": v(1130.3, -127) * mm});
            skLineSegment(sketch, "E229.1.0.1", {"start": v(1130.3, -355.6) * mm, "end": v(1206.5, -355.6) * mm});
            skLineSegment(sketch, "E229.1.0.2", {"start": v(1130.3, -127) * mm, "end": v(1206.5, -127) * mm});
            skLineSegment(sketch, "E229.1.0.3", {"start": v(1206.5, -355.6) * mm, "end": v(1206.5, -127) * mm});
            skCircle(sketch, "E229.1.0.4", {"center": v(1168.4, -171.45) * mm, "radius": 11.11 * mm});
            skCircle(sketch, "E229.1.0.5", {"center": v(1168.4, -311.15) * mm, "radius": 11.11 * mm});
            skLineSegment(sketch, "E229.direction1", {"start": v(-1206.5, -355.6) * mm, "end": v(1130.3, -355.6) * mm, "construction": true});
            skLineSegment(sketch, "E230.1.0.1", {"start": v(2578.1, -355.6) * mm, "end": v(2578.1, -127) * mm});
            skLineSegment(sketch, "E230.1.0.2", {"start": v(2654.3, -355.6) * mm, "end": v(2654.3, -127) * mm});
            skCircle(sketch, "E230.1.0.3", {"center": v(2616.2, -311.15) * mm, "radius": 11.11 * mm});
            skCircle(sketch, "E230.1.0.4", {"center": v(2616.2, -171.45) * mm, "radius": 11.11 * mm});
            skLineSegment(sketch, "E230.1.0.5", {"start": v(2578.1, -355.6) * mm, "end": v(2654.3, -355.6) * mm});
            skLineSegment(sketch, "E230.1.0.6", {"start": v(2578.1, -127) * mm, "end": v(2654.3, -127) * mm});
            skLineSegment(sketch, "E230.direction1", {"start": v(1320.8, -241.3) * mm, "end": v(2768.6, -241.3) * mm, "construction": true});
            skSolve(sketch);
        }
        {
            var Q0;
            Q0=qSketchRegion(id+"F15",true);
            extrude(context, id + "F16", {"entities" : qUnion([Q0]), "operationType" : NewBodyOperationType.ADD, "depth" : 19.05 * mm});
        }
        {
            var Q0;
            Q0=makeQuery(id+"F12.opExtrude","SWEPT_FACE",FACE,{"disambiguationData":[OSD([sQuery(id+"F11.wireOp",EDGE,"E173.MirrorCS")])]});
            var sketch = newSketch(context, id + "F17", { "sketchPlane" : qUnion([Q0])});
            skLineSegment(sketch, "E231", {"start": v(0, -262.73) * mm, "end": v(0, 1224.7) * mm, "construction": true});
            skLineSegment(sketch, "E232.0", {"start": v(-1320.8, 0) * mm, "end": v(1320.8, 0) * mm, "construction": true});
            skLineSegment(sketch, "E233.0", {"start": v(-1320.8, 231.9) * mm, "end": v(1320.8, 231.9) * mm, "construction": true});
            skLineSegment(sketch, "E234.0", {"start": v(-1187.45, -262.73) * mm, "end": v(-1187.45, 1224.7) * mm, "construction": true});
            skLineSegment(sketch, "E235.0", {"start": v(-1320.8, 333.5) * mm, "end": v(1320.8, 333.5) * mm, "construction": true});
            skLineSegment(sketch, "E236.bottom", {"start": v(-1289.05, 435.1) * mm, "end": v(-1085.85, 435.1) * mm});
            skLineSegment(sketch, "E236.top", {"start": v(-1289.05, 231.9) * mm, "end": v(-1085.85, 231.9) * mm});
            skLineSegment(sketch, "E236.left", {"start": v(-1289.05, 435.1) * mm, "end": v(-1289.05, 424.05) * mm});
            skLineSegment(sketch, "E236.right", {"start": v(-1085.85, 435.1) * mm, "end": v(-1085.85, 424.05) * mm});
            skPoint(sketch, "E236.middle", {"position": v(-1187.45, 333.5) * mm});
            skLineSegment(sketch, "E237.0", {"start": v(-1289.05, 424.05) * mm, "end": v(-1197.36, 424.05) * mm});
            skLineSegment(sketch, "E238.MirrorCS", {"start": v(-1289.05, 242.95) * mm, "end": v(-1197.36, 242.95) * mm});
            skLineSegment(sketch, "E239.0", {"start": v(-1183.9, 249.3) * mm, "end": v(-1183.9, 417.7) * mm});
            skLineSegment(sketch, "E240.MirrorCS", {"start": v(-1191, 249.3) * mm, "end": v(-1191, 417.7) * mm});
            skLineSegment(sketch, "E241", {"start": v(-1177.54, 424.05) * mm, "end": v(-1085.85, 424.05) * mm});
            skLineSegment(sketch, "E242", {"start": v(-1177.54, 242.95) * mm, "end": v(-1085.85, 242.95) * mm});
            skPoint(sketch, "E243.newPointB", {"position": v(-1191, 1224.7) * mm});
            skArc(sketch, "E243.filletArc", {"start": v(-1191, 417.7) * mm, "mid": v(-1192.87, 422.2) * mm, "end": v(-1197.36, 424.05) * mm});
            skPoint(sketch, "E244.newPointA", {"position": v(-1191, -262.73) * mm});
            skArc(sketch, "E244.filletArc", {"start": v(-1197.36, 242.95) * mm, "mid": v(-1192.87, 244.81) * mm, "end": v(-1191, 249.3) * mm});
            skPoint(sketch, "E245.newPointA", {"position": v(-1183.9, -262.73) * mm});
            skArc(sketch, "E245.filletArc", {"start": v(-1183.9, 249.3) * mm, "mid": v(-1182.03, 244.81) * mm, "end": v(-1177.54, 242.95) * mm});
            skPoint(sketch, "E246.newPointB", {"position": v(-1183.9, 1224.7) * mm});
            skArc(sketch, "E246.filletArc", {"start": v(-1177.54, 424.05) * mm, "mid": v(-1182.03, 422.2) * mm, "end": v(-1183.9, 417.7) * mm});
            skLineSegment(sketch, "E247.trimOffspring", {"start": v(-1289.05, 242.95) * mm, "end": v(-1289.05, 231.9) * mm});
            skLineSegment(sketch, "E248.trimOffspring", {"start": v(-1085.85, 242.95) * mm, "end": v(-1085.85, 231.9) * mm});
            skArc(sketch, "E249.MirrorCS", {"start": v(1177.54, 424.05) * mm, "mid": v(1182.03, 422.2) * mm, "end": v(1183.9, 417.7) * mm});
            skArc(sketch, "E250.MirrorCS", {"start": v(1183.9, 249.3) * mm, "mid": v(1182.03, 244.81) * mm, "end": v(1177.54, 242.95) * mm});
            skArc(sketch, "E251.MirrorCS", {"start": v(1197.36, 242.95) * mm, "mid": v(1192.87, 244.81) * mm, "end": v(1191, 249.3) * mm});
            skArc(sketch, "E252.MirrorCS", {"start": v(1191, 417.7) * mm, "mid": v(1192.87, 422.2) * mm, "end": v(1197.36, 424.05) * mm});
            skLineSegment(sketch, "E253.MirrorCS", {"start": v(1085.85, 242.95) * mm, "end": v(1085.85, 231.9) * mm});
            skLineSegment(sketch, "E254.MirrorCS", {"start": v(1183.9, 249.3) * mm, "end": v(1183.9, 417.7) * mm});
            skLineSegment(sketch, "E255.MirrorCS", {"start": v(1289.05, 242.95) * mm, "end": v(1289.05, 231.9) * mm});
            skLineSegment(sketch, "E256.MirrorCS", {"start": v(1085.85, 435.1) * mm, "end": v(1085.85, 424.05) * mm});
            skLineSegment(sketch, "E257.MirrorCS", {"start": v(1289.05, 435.1) * mm, "end": v(1289.05, 424.05) * mm});
            skLineSegment(sketch, "E258.MirrorCS", {"start": v(1289.05, 242.95) * mm, "end": v(1197.36, 242.95) * mm});
            skLineSegment(sketch, "E259.MirrorCS", {"start": v(1289.05, 424.05) * mm, "end": v(1197.36, 424.05) * mm});
            skLineSegment(sketch, "E260.MirrorCS", {"start": v(1289.05, 435.1) * mm, "end": v(1085.85, 435.1) * mm});
            skLineSegment(sketch, "E261.MirrorCS", {"start": v(1177.54, 424.05) * mm, "end": v(1085.85, 424.05) * mm});
            skLineSegment(sketch, "E262.MirrorCS", {"start": v(1289.05, 231.9) * mm, "end": v(1085.85, 231.9) * mm});
            skLineSegment(sketch, "E263.MirrorCS", {"start": v(1177.54, 242.95) * mm, "end": v(1085.85, 242.95) * mm});
            skLineSegment(sketch, "E264.MirrorCS", {"start": v(1191, 249.3) * mm, "end": v(1191, 417.7) * mm});
            skPoint(sketch, "E265.MirrorP", {"position": v(1187.45, 333.5) * mm});
            skSolve(sketch);
        }
        {
            var Q0;
            Q0=qSketchRegion(id+"F17",true);
            extrude(context, id + "F18", {"entities" : qUnion([Q0]), "depth" : 401.57 * mm});
        }
        {
            var Q0;
            Q0=makeQuery(id+"F18.opExtrude","SWEPT_FACE",FACE,{"disambiguationData":[OSD([sQuery(id+"F17.wireOp",EDGE,"E236.bottom")])]});
            var sketch = newSketch(context, id + "F19", { "sketchPlane" : qUnion([Q0])});
            skLineSegment(sketch, "E266.bottom", {"start": v(-1289.05, -649.22) * mm, "end": v(-1278, -649.22) * mm});
            skLineSegment(sketch, "E266.top", {"start": v(-1289.05, -446.02) * mm, "end": v(-1278, -446.02) * mm});
            skLineSegment(sketch, "E266.left", {"start": v(-1289.05, -649.22) * mm, "end": v(-1289.05, -446.02) * mm});
            skLineSegment(sketch, "E266.right", {"start": v(-1085.85, -649.22) * mm, "end": v(-1085.85, -446.02) * mm});
            skLineSegment(sketch, "E267", {"start": v(-1187.45, -446.02) * mm, "end": v(-1187.45, -700.9) * mm, "construction": true});
            skLineSegment(sketch, "E268", {"start": v(-1289.05, -547.62) * mm, "end": v(-1023.84, -547.62) * mm, "construction": true});
            skLineSegment(sketch, "E269.0", {"start": v(-1278, -649.22) * mm, "end": v(-1278, -557.53) * mm});
            skLineSegment(sketch, "E270.MirrorCS", {"start": v(-1096.9, -649.22) * mm, "end": v(-1096.9, -557.53) * mm});
            skLineSegment(sketch, "E271.0", {"start": v(-1271.65, -551.18) * mm, "end": v(-1103.25, -551.18) * mm});
            skLineSegment(sketch, "E272.MirrorCS", {"start": v(-1271.65, -544.07) * mm, "end": v(-1103.25, -544.07) * mm});
            skPoint(sketch, "E273.orphan", {"position": v(-1023.84, -551.18) * mm});
            skPoint(sketch, "E274.orphan", {"position": v(-1023.84, -544.07) * mm});
            skLineSegment(sketch, "E275.trimOffspring", {"start": v(-1096.9, -537.72) * mm, "end": v(-1096.9, -446.02) * mm});
            skPoint(sketch, "E276.orphan", {"position": v(-1289.05, -544.07) * mm});
            skLineSegment(sketch, "E277.trimOffspring", {"start": v(-1278, -537.72) * mm, "end": v(-1278, -446.02) * mm});
            skPoint(sketch, "E278.orphan", {"position": v(-1289.05, -551.18) * mm});
            skLineSegment(sketch, "E279.trimOffspring", {"start": v(-1096.9, -446.02) * mm, "end": v(-1085.85, -446.02) * mm});
            skLineSegment(sketch, "E280.trimOffspring", {"start": v(-1096.9, -649.22) * mm, "end": v(-1085.85, -649.22) * mm});
            skPoint(sketch, "E281.visualSharp", {"position": v(-1278, -544.07) * mm});
            skArc(sketch, "E281.filletArc", {"start": v(-1278, -537.72) * mm, "mid": v(-1276.14, -542.2) * mm, "end": v(-1271.65, -544.07) * mm});
            skPoint(sketch, "E282.visualSharp", {"position": v(-1278, -551.18) * mm});
            skArc(sketch, "E282.filletArc", {"start": v(-1271.65, -551.18) * mm, "mid": v(-1276.14, -553.04) * mm, "end": v(-1278, -557.53) * mm});
            skPoint(sketch, "E283.visualSharp", {"position": v(-1096.9, -551.18) * mm});
            skArc(sketch, "E283.filletArc", {"start": v(-1096.9, -557.53) * mm, "mid": v(-1098.76, -553.04) * mm, "end": v(-1103.25, -551.18) * mm});
            skPoint(sketch, "E284.visualSharp", {"position": v(-1096.9, -544.07) * mm});
            skArc(sketch, "E284.filletArc", {"start": v(-1103.25, -544.07) * mm, "mid": v(-1098.76, -542.2) * mm, "end": v(-1096.9, -537.72) * mm});
            skArc(sketch, "E285.MirrorCS", {"start": v(1271.65, -551.18) * mm, "mid": v(1276.14, -553.04) * mm, "end": v(1278, -557.53) * mm});
            skArc(sketch, "E286.MirrorCS", {"start": v(1278, -537.72) * mm, "mid": v(1276.14, -542.2) * mm, "end": v(1271.65, -544.07) * mm});
            skArc(sketch, "E287.MirrorCS", {"start": v(1096.9, -557.53) * mm, "mid": v(1098.76, -553.04) * mm, "end": v(1103.25, -551.18) * mm});
            skArc(sketch, "E288.MirrorCS", {"start": v(1103.25, -544.07) * mm, "mid": v(1098.76, -542.2) * mm, "end": v(1096.9, -537.72) * mm});
            skLineSegment(sketch, "E289.MirrorCS", {"start": v(1289.05, -547.62) * mm, "end": v(1023.84, -547.62) * mm, "construction": true});
            skLineSegment(sketch, "E290.MirrorCS", {"start": v(1096.9, -649.22) * mm, "end": v(1085.85, -649.22) * mm});
            skLineSegment(sketch, "E291.MirrorCS", {"start": v(1289.05, -649.22) * mm, "end": v(1278, -649.22) * mm});
            skLineSegment(sketch, "E292.MirrorCS", {"start": v(1289.05, -446.02) * mm, "end": v(1278, -446.02) * mm});
            skPoint(sketch, "E293.MirrorP", {"position": v(1096.9, -551.18) * mm});
            skLineSegment(sketch, "E294.MirrorCS", {"start": v(1096.9, -446.02) * mm, "end": v(1085.85, -446.02) * mm});
            skPoint(sketch, "E295.MirrorP", {"position": v(1289.05, -544.07) * mm});
            skPoint(sketch, "E296.MirrorP", {"position": v(1278, -551.18) * mm});
            skLineSegment(sketch, "E297.MirrorCS", {"start": v(1271.65, -551.18) * mm, "end": v(1103.25, -551.18) * mm});
            skLineSegment(sketch, "E298.MirrorCS", {"start": v(1289.05, -649.22) * mm, "end": v(1289.05, -446.02) * mm});
            skPoint(sketch, "E299.MirrorP", {"position": v(1289.05, -551.18) * mm});
            skLineSegment(sketch, "E300.MirrorCS", {"start": v(1085.85, -649.22) * mm, "end": v(1085.85, -446.02) * mm});
            skPoint(sketch, "E301.MirrorP", {"position": v(1278, -544.07) * mm});
            skLineSegment(sketch, "E302.MirrorCS", {"start": v(1096.9, -649.22) * mm, "end": v(1096.9, -557.53) * mm});
            skLineSegment(sketch, "E303.MirrorCS", {"start": v(1278, -537.72) * mm, "end": v(1278, -446.02) * mm});
            skLineSegment(sketch, "E304.MirrorCS", {"start": v(1278, -649.22) * mm, "end": v(1278, -557.53) * mm});
            skLineSegment(sketch, "E305.MirrorCS", {"start": v(1271.65, -544.07) * mm, "end": v(1103.25, -544.07) * mm});
            skPoint(sketch, "E306.MirrorP", {"position": v(1096.9, -544.07) * mm});
            skPoint(sketch, "E307.MirrorP", {"position": v(1023.84, -544.07) * mm});
            skLineSegment(sketch, "E308.MirrorCS", {"start": v(1096.9, -537.72) * mm, "end": v(1096.9, -446.02) * mm});
            skLineSegment(sketch, "E309.MirrorCS", {"start": v(1187.45, -446.02) * mm, "end": v(1187.45, -700.9) * mm, "construction": true});
            skPoint(sketch, "E310.MirrorP", {"position": v(1023.84, -551.18) * mm});
            skSolve(sketch);
        }
        {
            var Q0;
            Q0=qSketchRegion(id+"F19",true);
            extrude(context, id + "F20", {"entities" : qUnion([Q0]), "depth" : 292.1 * mm});
        }
        {
            var Q0;
            Q0=makeQuery(id+"F20.opExtrude","CAP_FACE",FACE,{"disambiguationData":[OSD([sQuery(id+"F19.wireOp",EDGE,"E266.bottom"),sQuery(id+"F19.wireOp",EDGE,"E266.top"),sQuery(id+"F19.wireOp",EDGE,"E266.left"),sQuery(id+"F19.wireOp",EDGE,"E266.right"),sQuery(id+"F19.wireOp",EDGE,"E269.0"),sQuery(id+"F19.wireOp",EDGE,"E270.MirrorCS"),sQuery(id+"F19.wireOp",EDGE,"E271.0"),sQuery(id+"F19.wireOp",EDGE,"E272.MirrorCS"),sQuery(id+"F19.wireOp",EDGE,"E275.trimOffspring"),sQuery(id+"F19.wireOp",EDGE,"E277.trimOffspring"),sQuery(id+"F19.wireOp",EDGE,"E279.trimOffspring"),sQuery(id+"F19.wireOp",EDGE,"E280.trimOffspring"),sQuery(id+"F19.wireOp",EDGE,"E281.filletArc"),sQuery(id+"F19.wireOp",EDGE,"E282.filletArc"),sQuery(id+"F19.wireOp",EDGE,"E283.filletArc"),sQuery(id+"F19.wireOp",EDGE,"E284.filletArc")])],"isStart":false});
            var sketch = newSketch(context, id + "F21", { "sketchPlane" : qUnion([Q0])});
            skLineSegment(sketch, "E311.0", {"start": v(-1289.05, -649.22) * mm, "end": v(-1289.05, -446.02) * mm, "construction": true});
            skLineSegment(sketch, "E312.0", {"start": v(-1085.85, -649.22) * mm, "end": v(-1085.85, -446.02) * mm, "construction": true});
            skLineSegment(sketch, "E313", {"start": v(-1289.05, -547.62) * mm, "end": v(-1085.85, -547.62) * mm, "construction": true});
            skLineSegment(sketch, "E314.bottom", {"start": v(-1301.75, -433.32) * mm, "end": v(-1073.15, -433.32) * mm});
            skLineSegment(sketch, "E314.top", {"start": v(-1301.75, -661.92) * mm, "end": v(-1073.15, -661.92) * mm});
            skLineSegment(sketch, "E314.left", {"start": v(-1301.75, -433.32) * mm, "end": v(-1301.75, -661.92) * mm});
            skLineSegment(sketch, "E314.right", {"start": v(-1073.15, -433.32) * mm, "end": v(-1073.15, -661.92) * mm});
            skPoint(sketch, "E314.middle", {"position": v(-1187.45, -547.62) * mm});
            skLineSegment(sketch, "E315", {"start": v(-1187.45, -433.32) * mm, "end": v(-1187.45, -661.92) * mm, "construction": true});
            skLineSegment(sketch, "E316.0", {"start": v(-1289.05, -477.77) * mm, "end": v(-1085.85, -477.77) * mm, "construction": true});
            skCircle(sketch, "E317", {"center": v(-1187.45, -477.77) * mm, "radius": 11.11 * mm});
            skCircle(sketch, "E318.MirrorC", {"center": v(-1187.45, -617.47) * mm, "radius": 11.11 * mm});
            skCircle(sketch, "E319.MirrorC", {"center": v(1187.45, -617.47) * mm, "radius": 11.11 * mm});
            skCircle(sketch, "E320.MirrorC", {"center": v(1187.45, -477.77) * mm, "radius": 11.11 * mm});
            skLineSegment(sketch, "E321.MirrorCS", {"start": v(1289.05, -477.77) * mm, "end": v(1085.85, -477.77) * mm, "construction": true});
            skLineSegment(sketch, "E322.MirrorCS", {"start": v(1289.05, -547.62) * mm, "end": v(1085.85, -547.62) * mm, "construction": true});
            skLineSegment(sketch, "E323.MirrorCS", {"start": v(1289.05, -649.22) * mm, "end": v(1289.05, -446.02) * mm, "construction": true});
            skLineSegment(sketch, "E324.MirrorCS", {"start": v(1187.45, -433.32) * mm, "end": v(1187.45, -661.92) * mm, "construction": true});
            skPoint(sketch, "E325.MirrorP", {"position": v(1187.45, -547.62) * mm});
            skLineSegment(sketch, "E326.MirrorCS", {"start": v(1073.15, -433.32) * mm, "end": v(1073.15, -661.92) * mm});
            skLineSegment(sketch, "E327.MirrorCS", {"start": v(1301.75, -661.92) * mm, "end": v(1073.15, -661.92) * mm});
            skLineSegment(sketch, "E328.MirrorCS", {"start": v(1301.75, -433.32) * mm, "end": v(1073.15, -433.32) * mm});
            skLineSegment(sketch, "E329.MirrorCS", {"start": v(1085.85, -649.22) * mm, "end": v(1085.85, -446.02) * mm, "construction": true});
            skLineSegment(sketch, "E330.MirrorCS", {"start": v(1301.75, -433.32) * mm, "end": v(1301.75, -661.92) * mm});
            skSolve(sketch);
        }
        {
            var Q0;
            Q0=qSketchRegion(id+"F21",true);
            extrude(context, id + "F22", {"entities" : qUnion([Q0]), "depth" : 19.05 * mm});
        }
        {
            var Q0;
            Q0=makeQuery(id+"F20.opExtrude","SWEPT_FACE",FACE,{"disambiguationData":[OSD([sQuery(id+"F19.wireOp",EDGE,"E266.right")])]});
            var sketch = newSketch(context, id + "F23", { "sketchPlane" : qUnion([Q0])});
            skLineSegment(sketch, "E331.0.0", {"start": v(-649.22, 435.1) * mm, "end": v(-446.02, 435.1) * mm, "construction": true});
            skLineSegment(sketch, "E331.0.1", {"start": v(-446.02, 435.1) * mm, "end": v(-446.02, 727.2) * mm, "construction": true});
            skLineSegment(sketch, "E331.0.2", {"start": v(-446.02, 727.2) * mm, "end": v(-649.22, 727.2) * mm, "construction": true});
            skLineSegment(sketch, "E331.0.3", {"start": v(-649.22, 727.2) * mm, "end": v(-649.22, 435.1) * mm, "construction": true});
            skLineSegment(sketch, "E332.0", {"start": v(-446.02, 574.8) * mm, "end": v(-649.22, 574.8) * mm, "construction": true});
            skLineSegment(sketch, "E333", {"start": v(-547.62, 574.8) * mm, "end": v(-547.62, 602) * mm, "construction": true});
            skCircle(sketch, "E334", {"center": v(-547.62, 574.8) * mm, "radius": 44.45 * mm});
            skCircle(sketch, "E335.0", {"center": v(-547.62, 574.8) * mm, "radius": 38.96 * mm});
            skSolve(sketch);
        }
        {
            var Q0;
            Q0=qSketchRegion(id+"F23",true);
            extrude(context, id + "F24", {"entities" : qUnion([Q0]), "depth" : 2171.7 * mm});
        }
        {
            var Q0;
            Q0=makeQuery(id+"F16.opExtrude","CAP_FACE",FACE,{"disambiguationData":[OSD([sQuery(id+"F15.wireOp",EDGE,"E229.1.0.0"),sQuery(id+"F15.wireOp",EDGE,"E229.1.0.1"),sQuery(id+"F15.wireOp",EDGE,"E229.1.0.2"),sQuery(id+"F15.wireOp",EDGE,"E229.1.0.3"),sQuery(id+"F15.wireOp",EDGE,"E229.1.0.4"),sQuery(id+"F15.wireOp",EDGE,"E229.1.0.5")])],"isStart":false});
            var sketch = newSketch(context, id + "F25", { "sketchPlane" : qUnion([Q0])});
            skLineSegment(sketch, "E336.0.0", {"start": v(1130.3, -127) * mm, "end": v(1130.3, -355.6) * mm});
            skLineSegment(sketch, "E336.0.1", {"start": v(1130.3, -355.6) * mm, "end": v(1206.5, -355.6) * mm});
            skLineSegment(sketch, "E336.0.2", {"start": v(1206.5, -355.6) * mm, "end": v(1206.5, -127) * mm});
            skLineSegment(sketch, "E336.0.3", {"start": v(1206.5, -127) * mm, "end": v(1130.3, -127) * mm});
            skCircle(sketch, "E337.0", {"center": v(1168.4, -311.15) * mm, "radius": 11.11 * mm});
            skCircle(sketch, "E338.0", {"center": v(1168.4, -171.45) * mm, "radius": 11.11 * mm});
            skLineSegment(sketch, "E339.0.0", {"start": v(2578.1, -127) * mm, "end": v(2578.1, -355.6) * mm});
            skLineSegment(sketch, "E339.0.1", {"start": v(2578.1, -355.6) * mm, "end": v(2654.3, -355.6) * mm});
            skLineSegment(sketch, "E339.0.2", {"start": v(2654.3, -355.6) * mm, "end": v(2654.3, -127) * mm});
            skLineSegment(sketch, "E339.0.3", {"start": v(2654.3, -127) * mm, "end": v(2578.1, -127) * mm});
            skCircle(sketch, "E340.0", {"center": v(2616.2, -171.45) * mm, "radius": 11.11 * mm});
            skCircle(sketch, "E341.0", {"center": v(2616.2, -311.15) * mm, "radius": 11.11 * mm});
            skSolve(sketch);
        }
        {
            var Q0;
            Q0=qSketchRegion(id+"F25",true);
            extrude(context, id + "F26", {"entities" : qUnion([Q0]), "depth" : 19 * mm});
        }
        {
            var Q0;
            {var subQ7=sQuery(id+"F11.wireOp",EDGE,"E174.trimOffspring");var subQ14=sQuery(id+"F11.wireOp",EDGE,"E169.top");Q0=makeQuery(id+"F16.boolean.opBoolean","SPLIT",FACE,{"disambiguationData":[TD([makeQuery(id+"F12.opExtrude","SWEPT_FACE",FACE,{"disambiguationData":[OSD([subQ7])]})])],"derivedFrom":makeQuery(id+"F12.opExtrude","SWEPT_FACE",FACE,{"disambiguationData":[OSD([subQ14])]})});}
            cPlane(context, id + "F27", {"entities" : qUnion([Q0]), "cplaneType" : CPlaneType.OFFSET, "offset" : 108 * mm, "width" : 150 * mm, "height" : 150 * mm});
        }
        {
            var Q0;
            Q0=qCreatedBy(id+"F27.planeOp",FACE);
            var sketch = newSketch(context, id + "F28", { "sketchPlane" : qUnion([Q0])});
            skLineSegment(sketch, "E342.0", {"start": v(2692.4, -1524.13) * mm, "end": v(2692.4, 788.61) * mm, "construction": true});
            skPoint(sketch, "E343.orphan", {"position": v(2692.4, -114.3) * mm});
            skPoint(sketch, "E344.orphan", {"position": v(2692.4, -368.3) * mm});
            skLineSegment(sketch, "E345.0", {"start": v(948.9, -1524.13) * mm, "end": v(948.9, 788.61) * mm, "construction": true});
            skLineSegment(sketch, "E346.0", {"start": v(1023.9, -1524.13) * mm, "end": v(1023.9, 788.61) * mm, "construction": true});
            skLineSegment(sketch, "E347.0", {"start": v(-1460.5, -368.3) * mm, "end": v(-1460.5, -114.3) * mm, "construction": true});
            skLineSegment(sketch, "E348", {"start": v(-1460.5, -241.3) * mm, "end": v(2900.96, -241.3) * mm, "construction": true});
            skPoint(sketch, "E348.endSnap0", {"position": v(-1460.5, -241.3) * mm});
            skLineSegment(sketch, "E349.bottom", {"start": v(948.9, -51.3) * mm, "end": v(1098.9, -51.3) * mm});
            skLineSegment(sketch, "E349.top", {"start": v(948.9, -431.3) * mm, "end": v(1098.9, -431.3) * mm});
            skLineSegment(sketch, "E349.left", {"start": v(948.9, -51.3) * mm, "end": v(948.9, -431.3) * mm});
            skLineSegment(sketch, "E349.right", {"start": v(1098.9, -51.3) * mm, "end": v(1098.9, -431.3) * mm});
            skPoint(sketch, "E349.middle", {"position": v(1023.9, -241.3) * mm});
            skLineSegment(sketch, "E350.0", {"start": v(-1460.5, -86.3) * mm, "end": v(2900.96, -86.3) * mm, "construction": true});
            skCircle(sketch, "E351", {"center": v(1023.9, -86.3) * mm, "radius": 7.25 * mm});
            skCircle(sketch, "E352.MirrorC", {"center": v(1023.9, -396.3) * mm, "radius": 7.25 * mm});
            skPoint(sketch, "E353.1.0.0", {"position": v(1698.9, -241.3) * mm});
            skLineSegment(sketch, "E353.1.0.1", {"start": v(1773.9, -51.3) * mm, "end": v(1773.9, -431.3) * mm});
            skLineSegment(sketch, "E353.1.0.2", {"start": v(1623.9, -51.3) * mm, "end": v(1773.9, -51.3) * mm});
            skLineSegment(sketch, "E353.1.0.3", {"start": v(1623.9, -431.3) * mm, "end": v(1773.9, -431.3) * mm});
            skLineSegment(sketch, "E353.1.0.4", {"start": v(1623.9, -51.3) * mm, "end": v(1623.9, -431.3) * mm});
            skCircle(sketch, "E353.1.0.5", {"center": v(1698.9, -396.3) * mm, "radius": 7.25 * mm});
            skCircle(sketch, "E353.1.0.6", {"center": v(1698.9, -86.3) * mm, "radius": 7.25 * mm});
            skPoint(sketch, "E353.2.0.0", {"position": v(2373.9, -241.3) * mm});
            skLineSegment(sketch, "E353.2.0.1", {"start": v(2448.9, -51.3) * mm, "end": v(2448.9, -431.3) * mm});
            skLineSegment(sketch, "E353.2.0.2", {"start": v(2298.9, -51.3) * mm, "end": v(2448.9, -51.3) * mm});
            skLineSegment(sketch, "E353.2.0.3", {"start": v(2298.9, -431.3) * mm, "end": v(2448.9, -431.3) * mm});
            skLineSegment(sketch, "E353.2.0.4", {"start": v(2298.9, -51.3) * mm, "end": v(2298.9, -431.3) * mm});
            skCircle(sketch, "E353.2.0.5", {"center": v(2373.9, -396.3) * mm, "radius": 7.25 * mm});
            skCircle(sketch, "E353.2.0.6", {"center": v(2373.9, -86.3) * mm, "radius": 7.25 * mm});
            skLineSegment(sketch, "E353.direction1", {"start": v(1023.9, -241.3) * mm, "end": v(1698.9, -241.3) * mm, "construction": true});
            skPoint(sketch, "E354.0.3.0", {"position": v(3048.9, -241.3) * mm});
            skLineSegment(sketch, "E354.1.3.0", {"start": v(3123.9, -51.3) * mm, "end": v(3123.9, -431.3) * mm});
            skLineSegment(sketch, "E354.4.3.0", {"start": v(2973.9, -51.3) * mm, "end": v(3123.9, -51.3) * mm});
            skLineSegment(sketch, "E354.7.3.0", {"start": v(2973.9, -431.3) * mm, "end": v(3123.9, -431.3) * mm});
            skLineSegment(sketch, "E354.10.3.0", {"start": v(2973.9, -51.3) * mm, "end": v(2973.9, -431.3) * mm});
            skCircle(sketch, "E354.13.3.0", {"center": v(3048.9, -396.3) * mm, "radius": 7.25 * mm});
            skCircle(sketch, "E354.15.3.0", {"center": v(3048.9, -86.3) * mm, "radius": 7.25 * mm});
            skPoint(sketch, "E354.0.4.0", {"position": v(3723.9, -241.3) * mm});
            skLineSegment(sketch, "E354.1.4.0", {"start": v(3798.9, -51.3) * mm, "end": v(3798.9, -431.3) * mm});
            skLineSegment(sketch, "E354.4.4.0", {"start": v(3648.9, -51.3) * mm, "end": v(3798.9, -51.3) * mm});
            skLineSegment(sketch, "E354.7.4.0", {"start": v(3648.9, -431.3) * mm, "end": v(3798.9, -431.3) * mm});
            skLineSegment(sketch, "E354.10.4.0", {"start": v(3648.9, -51.3) * mm, "end": v(3648.9, -431.3) * mm});
            skCircle(sketch, "E354.13.4.0", {"center": v(3723.9, -396.3) * mm, "radius": 7.25 * mm});
            skCircle(sketch, "E354.15.4.0", {"center": v(3723.9, -86.3) * mm, "radius": 7.25 * mm});
            skSolve(sketch);
        }
        {
            var Q0;
            Q0=qSketchRegion(id+"F28",true);
            extrude(context, id + "F29", {"entities" : qUnion([Q0]), "oppositeDirection" : true, "depth" : 19 * mm});
        }
        {
            var Q0;
            Q0=makeQuery(id+"F26.opExtrude","SWEPT_FACE",FACE,{"disambiguationData":[OSD([sQuery(id+"F25.wireOp",EDGE,"E336.0.1")])]});
            var Q1;
            Q1=makeQuery(id+"F26.opExtrude","SWEPT_FACE",FACE,{"disambiguationData":[OSD([sQuery(id+"F25.wireOp",EDGE,"E336.0.3")])]});
            cPlane(context, id + "F30", {"entities" : qUnion([Q0, Q1]), "cplaneType" : CPlaneType.MID_PLANE, "offset" : 150 * mm, "width" : 150 * mm, "height" : 150 * mm});
        }
        {
            var Q0;
            Q0=qCreatedBy(id+"F10.planeOp",FACE);
            var sketch = newSketch(context, id + "F31", { "sketchPlane" : qUnion([Q0])});
            skLineSegment(sketch, "E355.0.0", {"start": v(-368.3, 231.65) * mm, "end": v(-368.3, 217.42) * mm, "construction": true});
            skLineSegment(sketch, "E355.0.1", {"start": v(-368.3, 217.42) * mm, "end": v(-114.3, 217.42) * mm, "construction": true});
            skLineSegment(sketch, "E355.0.2", {"start": v(-114.3, 217.42) * mm, "end": v(-114.3, 231.65) * mm, "construction": true});
            skLineSegment(sketch, "E355.0.3", {"start": v(-114.3, 231.65) * mm, "end": v(-228.6, 231.65) * mm, "construction": true});
            skArc(sketch, "E355.0.4", {"start": v(-228.6, 231.65) * mm, "mid": v(-233.1, 233.5) * mm, "end": v(-234.95, 238) * mm, "construction": true});
            skLineSegment(sketch, "E355.0.5", {"start": v(-234.95, 238) * mm, "end": v(-234.95, 450.85) * mm, "construction": true});
            skArc(sketch, "E355.0.6", {"start": v(-234.95, 450.85) * mm, "mid": v(-233.1, 455.34) * mm, "end": v(-228.6, 457.2) * mm, "construction": true});
            skLineSegment(sketch, "E355.0.7", {"start": v(-228.6, 457.2) * mm, "end": v(-114.3, 457.2) * mm, "construction": true});
            skLineSegment(sketch, "E355.0.8", {"start": v(-114.3, 457.2) * mm, "end": v(-114.3, 471.42) * mm, "construction": true});
            skLineSegment(sketch, "E355.0.9", {"start": v(-114.3, 471.42) * mm, "end": v(-368.3, 471.42) * mm, "construction": true});
            skLineSegment(sketch, "E355.0.10", {"start": v(-368.3, 471.42) * mm, "end": v(-368.3, 457.2) * mm, "construction": true});
            skLineSegment(sketch, "E355.0.11", {"start": v(-368.3, 457.2) * mm, "end": v(-254, 457.2) * mm, "construction": true});
            skArc(sketch, "E355.0.12", {"start": v(-254, 457.2) * mm, "mid": v(-249.5, 455.34) * mm, "end": v(-247.65, 450.85) * mm, "construction": true});
            skLineSegment(sketch, "E355.0.13", {"start": v(-247.65, 450.85) * mm, "end": v(-247.65, 238) * mm, "construction": true});
            skArc(sketch, "E355.0.14", {"start": v(-247.65, 238) * mm, "mid": v(-249.5, 233.5) * mm, "end": v(-254, 231.65) * mm, "construction": true});
            skLineSegment(sketch, "E355.0.15", {"start": v(-254, 231.65) * mm, "end": v(-368.3, 231.65) * mm, "construction": true});
            skLineSegment(sketch, "E356.bottom", {"start": v(-368.3, 464.31) * mm, "end": v(-114.3, 464.31) * mm});
            skLineSegment(sketch, "E356.top", {"start": v(-368.3, 224.54) * mm, "end": v(-114.3, 224.54) * mm});
            skLineSegment(sketch, "E356.left", {"start": v(-368.3, 464.31) * mm, "end": v(-368.3, 224.54) * mm});
            skLineSegment(sketch, "E356.right", {"start": v(-114.3, 464.31) * mm, "end": v(-114.3, 224.54) * mm});
            skLineSegment(sketch, "E357", {"start": v(-368.3, 344.42) * mm, "end": v(-114.3, 344.42) * mm, "construction": true});
            skLineSegment(sketch, "E358.0", {"start": v(-368.3, 424.42) * mm, "end": v(-114.3, 424.42) * mm, "construction": true});
            skLineSegment(sketch, "E359.0", {"start": v(-318.3, 464.31) * mm, "end": v(-318.3, 224.54) * mm, "construction": true});
            skLineSegment(sketch, "E360.MirrorCS", {"start": v(-368.3, 264.42) * mm, "end": v(-114.3, 264.42) * mm, "construction": true});
            skCircle(sketch, "E361", {"center": v(-318.3, 424.42) * mm, "radius": 10 * mm});
            skCircle(sketch, "E362", {"center": v(-318.3, 344.42) * mm, "radius": 10 * mm});
            skCircle(sketch, "E363", {"center": v(-318.3, 264.42) * mm, "radius": 10 * mm});
            skLineSegment(sketch, "E364", {"start": v(-241.3, 471.42) * mm, "end": v(-241.3, 217.42) * mm, "construction": true});
            skCircle(sketch, "E365.MirrorC", {"center": v(-164.3, 264.42) * mm, "radius": 10 * mm});
            skCircle(sketch, "E366.MirrorC", {"center": v(-164.3, 424.42) * mm, "radius": 10 * mm});
            skCircle(sketch, "E367.MirrorC", {"center": v(-164.3, 344.42) * mm, "radius": 10 * mm});
            skSolve(sketch);
        }
        {
            var Q0;
            Q0=qSketchRegion(id+"F31",true);
            extrude(context, id + "F32", {"entities" : qUnion([Q0]), "depth" : 19 * mm});
        }
        {
            var Q0;
            Q0=makeQuery(id+"F32.opExtrude","CAP_FACE",FACE,{"disambiguationData":[OSD([sQuery(id+"F31.wireOp",EDGE,"E356.bottom"),sQuery(id+"F31.wireOp",EDGE,"E356.top"),sQuery(id+"F31.wireOp",EDGE,"E356.left"),sQuery(id+"F31.wireOp",EDGE,"E356.right"),sQuery(id+"F31.wireOp",EDGE,"E361"),sQuery(id+"F31.wireOp",EDGE,"E362"),sQuery(id+"F31.wireOp",EDGE,"E363"),sQuery(id+"F31.wireOp",EDGE,"E365.MirrorC"),sQuery(id+"F31.wireOp",EDGE,"E366.MirrorC"),sQuery(id+"F31.wireOp",EDGE,"E367.MirrorC")])],"isStart":false});
            var sketch = newSketch(context, id + "F33", { "sketchPlane" : qUnion([Q0])});
            skLineSegment(sketch, "E368.0.0", {"start": v(-114.3, 464.31) * mm, "end": v(-368.3, 464.31) * mm});
            skLineSegment(sketch, "E368.0.1", {"start": v(-368.3, 464.31) * mm, "end": v(-368.3, 224.54) * mm});
            skLineSegment(sketch, "E368.0.2", {"start": v(-368.3, 224.54) * mm, "end": v(-114.3, 224.54) * mm});
            skLineSegment(sketch, "E368.0.3", {"start": v(-114.3, 224.54) * mm, "end": v(-114.3, 464.31) * mm});
            skCircle(sketch, "E369.0", {"center": v(-318.3, 424.42) * mm, "radius": 10 * mm});
            skCircle(sketch, "E370.0", {"center": v(-318.3, 344.42) * mm, "radius": 10 * mm});
            skCircle(sketch, "E371.0", {"center": v(-318.3, 264.42) * mm, "radius": 10 * mm});
            skCircle(sketch, "E372.0", {"center": v(-164.3, 264.42) * mm, "radius": 10 * mm});
            skCircle(sketch, "E373.0", {"center": v(-164.3, 344.42) * mm, "radius": 10 * mm});
            skCircle(sketch, "E374.0", {"center": v(-164.3, 424.42) * mm, "radius": 10 * mm});
            skSolve(sketch);
        }
        {
            var Q0;
            Q0=qSketchRegion(id+"F33",true);
            extrude(context, id + "F34", {"entities" : qUnion([Q0]), "depth" : 19 * mm});
        }
        {
            var Q0;
            Q0=qCreatedBy(id+"F30.planeOp",FACE);
            var sketch = newSketch(context, id + "F35", { "sketchPlane" : qUnion([Q0])});
            skLineSegment(sketch, "E375.0", {"start": v(948.9, 560.42) * mm, "end": v(1098.9, 560.42) * mm, "construction": true});
            skLineSegment(sketch, "E376.0", {"start": v(2973.9, 560.42) * mm, "end": v(3123.9, 560.42) * mm, "construction": true});
            skLineSegment(sketch, "E377.0", {"start": v(3648.9, 560.42) * mm, "end": v(3798.9, 560.42) * mm, "construction": true});
            skLineSegment(sketch, "E378.0", {"start": v(2730.4, 464.31) * mm, "end": v(2730.4, 224.54) * mm, "construction": true});
            skLineSegment(sketch, "E379", {"start": v(948.9, 560.42) * mm, "end": v(3798.9, 560.42) * mm});
            skLineSegment(sketch, "E380.0", {"start": v(1130.3, 509.47) * mm, "end": v(1206.5, 509.47) * mm, "construction": true});
            skLineSegment(sketch, "E381", {"start": v(3798.9, 560.42) * mm, "end": v(3798.9, 224.54) * mm});
            skLineSegment(sketch, "E382", {"start": v(3798.9, 224.54) * mm, "end": v(2730.4, 224.54) * mm});
            skLineSegment(sketch, "E383", {"start": v(948.9, 560.42) * mm, "end": v(948.9, 509.47) * mm});
            skLineSegment(sketch, "E384", {"start": v(948.9, 509.47) * mm, "end": v(2720.4, 509.47) * mm});
            skLineSegment(sketch, "E385", {"start": v(2730.4, 499.47) * mm, "end": v(2730.4, 464.31) * mm});
            skLineSegment(sketch, "E386", {"start": v(2730.4, 464.31) * mm, "end": v(2730.4, 224.54) * mm});
            skPoint(sketch, "E387.visualSharp", {"position": v(2730.4, 509.47) * mm});
            skArc(sketch, "E387.filletArc", {"start": v(2730.4, 499.47) * mm, "mid": v(2727.47, 506.55) * mm, "end": v(2720.4, 509.47) * mm});
            skSolve(sketch);
        }
        {
            var Q0;
            Q0=qSketchRegion(id+"F35",true);
            extrude(context, id + "F36", {"entities" : qUnion([Q0]), "endBound" : BoundingType.SYMMETRIC, "depth" : 12.5 * mm});
        }
        {
            var Q0;
            Q0=makeQuery(id+"F26.opExtrude","SWEPT_FACE",FACE,{"disambiguationData":[OSD([sQuery(id+"F25.wireOp",EDGE,"E336.0.1")])]});
            var sketch = newSketch(context, id + "F37", { "sketchPlane" : qUnion([Q0])});
            skLineSegment(sketch, "E388.0.0", {"start": v(3798.9, 560.42) * mm, "end": v(948.9, 560.42) * mm});
            skLineSegment(sketch, "E388.0.1", {"start": v(948.9, 560.42) * mm, "end": v(948.9, 509.47) * mm});
            skLineSegment(sketch, "E388.0.2", {"start": v(948.9, 509.47) * mm, "end": v(2720.4, 509.47) * mm});
            skArc(sketch, "E388.0.3", {"start": v(2720.4, 509.47) * mm, "mid": v(2727.47, 506.55) * mm, "end": v(2730.4, 499.47) * mm});
            skLineSegment(sketch, "E388.0.4", {"start": v(2730.4, 499.47) * mm, "end": v(2730.4, 224.54) * mm});
            skLineSegment(sketch, "E388.0.5", {"start": v(2730.4, 224.54) * mm, "end": v(3798.9, 224.54) * mm});
            skLineSegment(sketch, "E388.0.6", {"start": v(3798.9, 224.54) * mm, "end": v(3798.9, 560.42) * mm});
            skSolve(sketch);
        }
        {
            var Q0;
            Q0=qSketchRegion(id+"F37",true);
            extrude(context, id + "F38", {"entities" : qUnion([Q0]), "endBound" : BoundingType.SYMMETRIC, "depth" : 12.5 * mm});
        }
        {
            var Q0;
            Q0=makeQuery(id+"F36.opExtrude","SWEPT_EDGE",EDGE,{"disambiguationData":[OSD([sQuery(id+"F35.wireOp",EDGE,"E381"),sQuery(id+"F35.wireOp",EDGE,"E382")])]});
            var Q1;
            Q1=makeQuery(id+"F38.opExtrude","SWEPT_EDGE",EDGE,{"disambiguationData":[OSD([sQuery(id+"F37.wireOp",EDGE,"E388.0.5"),sQuery(id+"F37.wireOp",EDGE,"E388.0.6")])]});
            chamfer(context, id + "F39", {"entities" : qUnion([Q0, Q1]), "chamferType" : ChamferType.TWO_OFFSETS, "width1" : 300 * mm, "oppositeDirection" : false, "width2" : 600 * mm, "tangentPropagation" : true});
        }
        {
            var Q0;
            Q0=makeQuery(id+"F38.opExtrude","SWEPT_BODY",BODY,{"disambiguationData":[OSD([sQuery(id+"F37.wireOp",EDGE,"E388.0.0"),sQuery(id+"F37.wireOp",EDGE,"E388.0.1"),sQuery(id+"F37.wireOp",EDGE,"E388.0.2"),sQuery(id+"F37.wireOp",EDGE,"E388.0.3"),sQuery(id+"F37.wireOp",EDGE,"E388.0.4"),sQuery(id+"F37.wireOp",EDGE,"E388.0.5"),sQuery(id+"F37.wireOp",EDGE,"E388.0.6")])]});
            var Q1;
            Q1=qCreatedBy(id+"F30.planeOp",FACE);
            mirror(context, id + "F40", {"entities" : qUnion([Q0]), "mirrorPlane" : qUnion([Q1])});
        }
        {
            var Q0;
            Q0=makeQuery(id+"F36.opExtrude","SWEPT_EDGE",EDGE,{"disambiguationData":[OSD([sQuery(id+"F35.wireOp",EDGE,"E383"),sQuery(id+"F35.wireOp",EDGE,"E384")])]});
            var Q1;
            Q1=makeQuery(id+"F40.opPattern","COPY",EDGE,{"derivedFrom":makeQuery(id+"F38.opExtrude","SWEPT_EDGE",EDGE,{"disambiguationData":[OSD([sQuery(id+"F37.wireOp",EDGE,"E388.0.1"),sQuery(id+"F37.wireOp",EDGE,"E388.0.2")])]}),"instanceName":"1"});
            var Q2;
            Q2=makeQuery(id+"F38.opExtrude","SWEPT_EDGE",EDGE,{"disambiguationData":[OSD([sQuery(id+"F37.wireOp",EDGE,"E388.0.1"),sQuery(id+"F37.wireOp",EDGE,"E388.0.2")])]});
            chamfer(context, id + "F41", {"entities" : qUnion([Q0, Q1, Q2]), "width" : 40 * mm, "tangentPropagation" : true});
        }
        {
            var Q0;
            Q0=makeQuery(id+"F38.opExtrude","SWEPT_BODY",BODY,{"disambiguationData":[OSD([sQuery(id+"F37.wireOp",EDGE,"E388.0.0"),sQuery(id+"F37.wireOp",EDGE,"E388.0.1"),sQuery(id+"F37.wireOp",EDGE,"E388.0.2"),sQuery(id+"F37.wireOp",EDGE,"E388.0.3"),sQuery(id+"F37.wireOp",EDGE,"E388.0.4"),sQuery(id+"F37.wireOp",EDGE,"E388.0.5"),sQuery(id+"F37.wireOp",EDGE,"E388.0.6")])]});
            var Q1;
            Q1=makeQuery(id+"F34.opExtrude","SWEPT_BODY",BODY,{"disambiguationData":[OSD([sQuery(id+"F33.wireOp",EDGE,"E368.0.0"),sQuery(id+"F33.wireOp",EDGE,"E368.0.1"),sQuery(id+"F33.wireOp",EDGE,"E368.0.2"),sQuery(id+"F33.wireOp",EDGE,"E368.0.3"),sQuery(id+"F33.wireOp",EDGE,"E369.0"),sQuery(id+"F33.wireOp",EDGE,"E370.0"),sQuery(id+"F33.wireOp",EDGE,"E371.0"),sQuery(id+"F33.wireOp",EDGE,"E372.0"),sQuery(id+"F33.wireOp",EDGE,"E373.0"),sQuery(id+"F33.wireOp",EDGE,"E374.0")])]});
            var Q2;
            Q2=makeQuery(id+"F29.opExtrude","SWEPT_BODY",BODY,{"disambiguationData":[OSD([sQuery(id+"F28.wireOp",EDGE,"E354.1.4.0"),sQuery(id+"F28.wireOp",EDGE,"E354.4.4.0"),sQuery(id+"F28.wireOp",EDGE,"E354.7.4.0"),sQuery(id+"F28.wireOp",EDGE,"E354.10.4.0"),sQuery(id+"F28.wireOp",EDGE,"E354.13.4.0"),sQuery(id+"F28.wireOp",EDGE,"E354.15.4.0")])]});
            var Q3;
            Q3=makeQuery(id+"F29.opExtrude","SWEPT_BODY",BODY,{"disambiguationData":[OSD([sQuery(id+"F28.wireOp",EDGE,"E354.1.3.0"),sQuery(id+"F28.wireOp",EDGE,"E354.4.3.0"),sQuery(id+"F28.wireOp",EDGE,"E354.7.3.0"),sQuery(id+"F28.wireOp",EDGE,"E354.10.3.0"),sQuery(id+"F28.wireOp",EDGE,"E354.13.3.0"),sQuery(id+"F28.wireOp",EDGE,"E354.15.3.0")])]});
            var Q4;
            Q4=makeQuery(id+"F29.opExtrude","SWEPT_BODY",BODY,{"disambiguationData":[OSD([sQuery(id+"F28.wireOp",EDGE,"E353.2.0.1"),sQuery(id+"F28.wireOp",EDGE,"E353.2.0.2"),sQuery(id+"F28.wireOp",EDGE,"E353.2.0.3"),sQuery(id+"F28.wireOp",EDGE,"E353.2.0.4"),sQuery(id+"F28.wireOp",EDGE,"E353.2.0.5"),sQuery(id+"F28.wireOp",EDGE,"E353.2.0.6")])]});
            var Q5;
            Q5=makeQuery(id+"F29.opExtrude","SWEPT_BODY",BODY,{"disambiguationData":[OSD([sQuery(id+"F28.wireOp",EDGE,"E353.1.0.1"),sQuery(id+"F28.wireOp",EDGE,"E353.1.0.2"),sQuery(id+"F28.wireOp",EDGE,"E353.1.0.3"),sQuery(id+"F28.wireOp",EDGE,"E353.1.0.4"),sQuery(id+"F28.wireOp",EDGE,"E353.1.0.5"),sQuery(id+"F28.wireOp",EDGE,"E353.1.0.6")])]});
            var Q6;
            Q6=makeQuery(id+"F29.opExtrude","SWEPT_BODY",BODY,{"disambiguationData":[OSD([sQuery(id+"F28.wireOp",EDGE,"E349.bottom"),sQuery(id+"F28.wireOp",EDGE,"E349.top"),sQuery(id+"F28.wireOp",EDGE,"E349.left"),sQuery(id+"F28.wireOp",EDGE,"E349.right"),sQuery(id+"F28.wireOp",EDGE,"E351"),sQuery(id+"F28.wireOp",EDGE,"E352.MirrorC")])]});
            var Q7;
            Q7=makeQuery(id+"F36.opExtrude","SWEPT_BODY",BODY,{"disambiguationData":[OSD([sQuery(id+"F35.wireOp",EDGE,"E379"),sQuery(id+"F35.wireOp",EDGE,"E381"),sQuery(id+"F35.wireOp",EDGE,"E382"),sQuery(id+"F35.wireOp",EDGE,"E383"),sQuery(id+"F35.wireOp",EDGE,"E384"),sQuery(id+"F35.wireOp",EDGE,"E385"),sQuery(id+"F35.wireOp",EDGE,"E386"),sQuery(id+"F35.wireOp",EDGE,"E387.filletArc")])]});
            var Q8;
            Q8=makeQuery(id+"F40.opPattern","COPY",BODY,{"derivedFrom":makeQuery(id+"F38.opExtrude","SWEPT_BODY",BODY,{"disambiguationData":[OSD([sQuery(id+"F37.wireOp",EDGE,"E388.0.0"),sQuery(id+"F37.wireOp",EDGE,"E388.0.1"),sQuery(id+"F37.wireOp",EDGE,"E388.0.2"),sQuery(id+"F37.wireOp",EDGE,"E388.0.3"),sQuery(id+"F37.wireOp",EDGE,"E388.0.4"),sQuery(id+"F37.wireOp",EDGE,"E388.0.5"),sQuery(id+"F37.wireOp",EDGE,"E388.0.6")])]}),"instanceName":"1"});
            var Q9;
            Q9=makeQuery(id+"F26.opExtrude","SWEPT_BODY",BODY,{"disambiguationData":[OSD([sQuery(id+"F25.wireOp",EDGE,"E336.0.0"),sQuery(id+"F25.wireOp",EDGE,"E336.0.1"),sQuery(id+"F25.wireOp",EDGE,"E336.0.2"),sQuery(id+"F25.wireOp",EDGE,"E336.0.3"),sQuery(id+"F25.wireOp",EDGE,"E337.0"),sQuery(id+"F25.wireOp",EDGE,"E338.0")])]});
            var Q10;
            Q10=makeQuery(id+"F26.opExtrude","SWEPT_BODY",BODY,{"disambiguationData":[OSD([sQuery(id+"F25.wireOp",EDGE,"E339.0.0"),sQuery(id+"F25.wireOp",EDGE,"E339.0.1"),sQuery(id+"F25.wireOp",EDGE,"E339.0.2"),sQuery(id+"F25.wireOp",EDGE,"E339.0.3"),sQuery(id+"F25.wireOp",EDGE,"E340.0"),sQuery(id+"F25.wireOp",EDGE,"E341.0")])]});
            booleanBodies(context, id + "F42", {"operationType" : BooleanOperationType.UNION, "tools" : qUnion([Q0, Q1, Q2, Q3, Q4, Q5, Q6, Q7, Q8, Q9, Q10])});
        }
        {
            var Q0;
            {var subQ0=makeQuery(id+"F38.opExtrude","SWEPT_FACE",FACE,{"disambiguationData":[OSD([sQuery(id+"F37.wireOp",EDGE,"E388.0.5")])]});Q0=makeQuery(id+"F42.opBoolean","MERGE",FACE,{"derivedFrom":[makeQuery(id+"F34.opExtrude","SWEPT_FACE",FACE,{"disambiguationData":[OSD([sQuery(id+"F33.wireOp",EDGE,"E368.0.2")])]}),makeQuery(id+"F36.opExtrude","SWEPT_FACE",FACE,{"disambiguationData":[OSD([sQuery(id+"F35.wireOp",EDGE,"E382")])]}),subQ0,makeQuery(id+"F40.opPattern","COPY",FACE,{"derivedFrom":subQ0,"instanceName":"1"})]});}
            var sketch = newSketch(context, id + "F43", { "sketchPlane" : qUnion([Q0])});
            skLineSegment(sketch, "E389.0.0", {"start": v(2730.4, 349.35) * mm, "end": v(3198.9, 349.35) * mm, "construction": true});
            skLineSegment(sketch, "E389.0.1", {"start": v(3198.9, 349.35) * mm, "end": v(3198.9, 361.85) * mm, "construction": true});
            skLineSegment(sketch, "E389.0.2", {"start": v(3198.9, 361.85) * mm, "end": v(2730.4, 361.85) * mm, "construction": true});
            skLineSegment(sketch, "E389.0.3", {"start": v(2730.4, 361.85) * mm, "end": v(2730.4, 368.3) * mm, "construction": true});
            skLineSegment(sketch, "E389.0.4", {"start": v(2730.4, 368.3) * mm, "end": v(2711.4, 368.3) * mm, "construction": true});
            skLineSegment(sketch, "E389.0.5", {"start": v(2711.4, 368.3) * mm, "end": v(2711.4, 114.3) * mm, "construction": true});
            skLineSegment(sketch, "E389.0.6", {"start": v(2711.4, 114.3) * mm, "end": v(2730.4, 114.3) * mm, "construction": true});
            skLineSegment(sketch, "E389.0.7", {"start": v(2730.4, 114.3) * mm, "end": v(2730.4, 120.75) * mm, "construction": true});
            skLineSegment(sketch, "E389.0.8", {"start": v(2730.4, 120.75) * mm, "end": v(3198.9, 120.75) * mm, "construction": true});
            skLineSegment(sketch, "E389.0.9", {"start": v(3198.9, 120.75) * mm, "end": v(3198.9, 133.25) * mm, "construction": true});
            skLineSegment(sketch, "E389.0.10", {"start": v(3198.9, 133.25) * mm, "end": v(2730.4, 133.25) * mm, "construction": true});
            skLineSegment(sketch, "E389.0.11", {"start": v(2730.4, 133.25) * mm, "end": v(2730.4, 235.05) * mm, "construction": true});
            skLineSegment(sketch, "E389.0.12", {"start": v(2730.4, 235.05) * mm, "end": v(3198.9, 235.05) * mm, "construction": true});
            skLineSegment(sketch, "E389.0.13", {"start": v(3198.9, 235.05) * mm, "end": v(3198.9, 247.55) * mm, "construction": true});
            skLineSegment(sketch, "E389.0.14", {"start": v(3198.9, 247.55) * mm, "end": v(2730.4, 247.55) * mm, "construction": true});
            skLineSegment(sketch, "E389.0.15", {"start": v(2730.4, 247.55) * mm, "end": v(2730.4, 349.35) * mm, "construction": true});
            skPoint(sketch, "E390.oppositeSnap0", {"position": v(3198.9, 127) * mm});
            skLineSegment(sketch, "E390.bottom", {"start": v(3198.9, 355.6) * mm, "end": v(3048.9, 355.6) * mm});
            skLineSegment(sketch, "E390.top", {"start": v(3198.9, 127) * mm, "end": v(3048.9, 127) * mm});
            skLineSegment(sketch, "E390.left", {"start": v(3198.9, 355.6) * mm, "end": v(3198.9, 127) * mm});
            skLineSegment(sketch, "E390.right", {"start": v(3048.9, 355.6) * mm, "end": v(3048.9, 127) * mm});
            skSolve(sketch);
        }
        {
            var Q0;
            Q0 = qSketchRegion(id + "F43", true);
            extrude(context, id + "F44", {"entities" : qUnion([Q0]), "operationType" : NewBodyOperationType.ADD, "depth" : 12.5 * mm});
        }
    });
